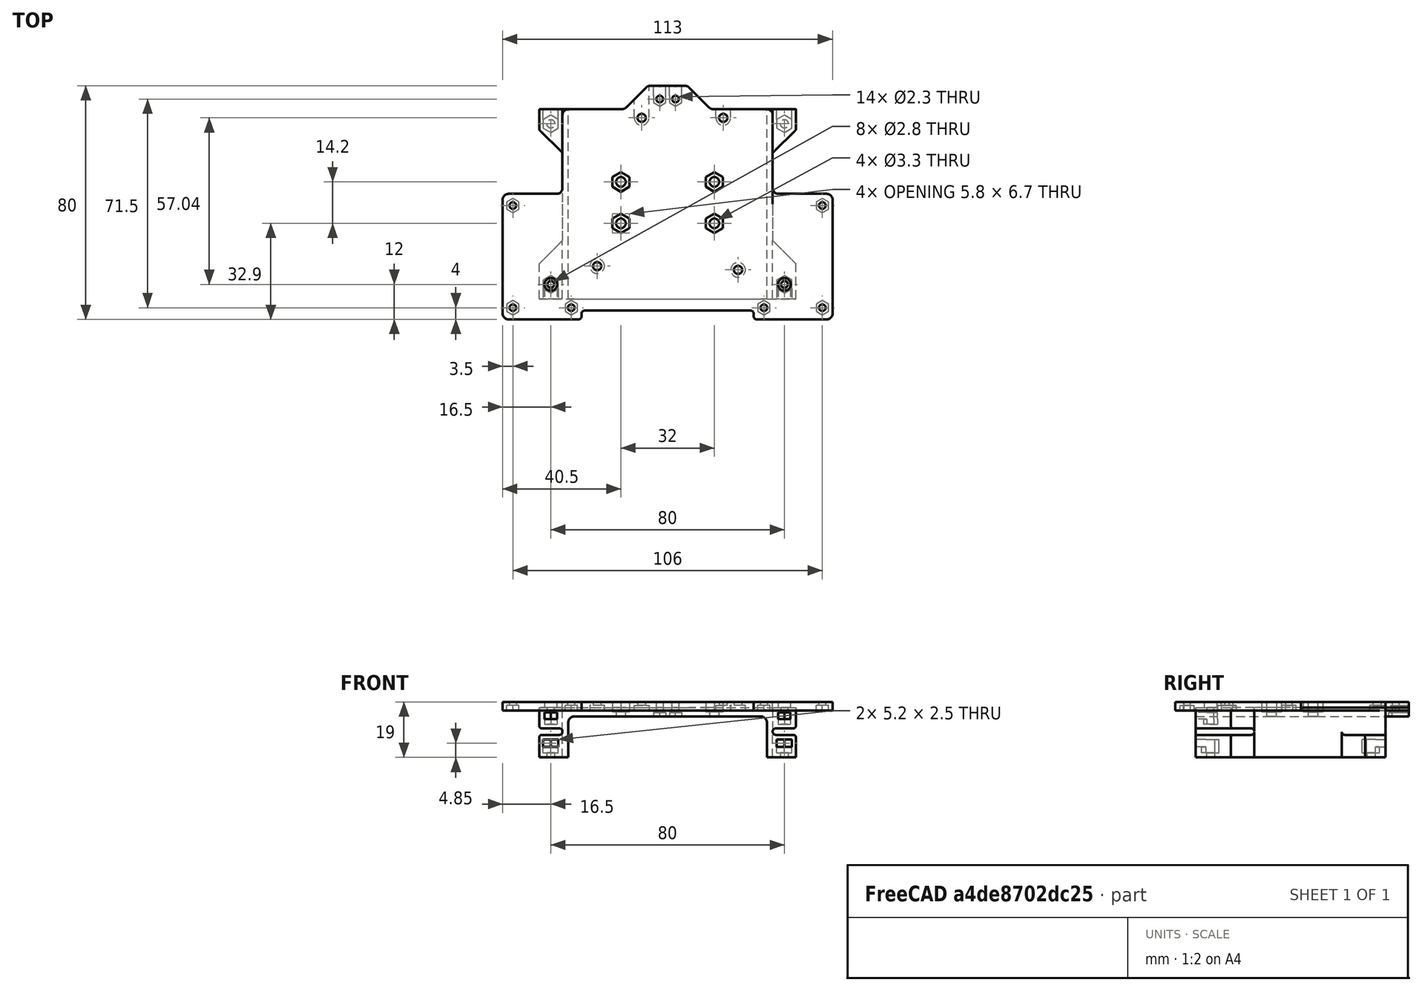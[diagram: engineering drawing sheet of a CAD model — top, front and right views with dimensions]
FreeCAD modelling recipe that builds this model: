
FCSTD DOCUMENT  (FreeCAD 0.19R24276 (Git))
Label: PB3D_TriPlate_BatBox
License: All rights reserved
LicenseURL: http://en.wikipedia.org/wiki/All_rights_reserved
objects: Sketcher::SketchObject×24, PartDesign::Pocket×18, PartDesign::Plane×7, PartDesign::Pad×2, PartDesign::Body×2, App::Part×2, Mesh::Feature×2, Spreadsheet::Sheet×1
note: 73 computed .brp shape members not serialized (recipe doc carries the construction recipe); baked Part::Feature solids carry a one-line shape summary decoded from their .brp

FEATURE [Spreadsheet::Sheet] Spreadsheet  label="params"
  cells = A2=M2 Bolt Clearances; C2=M2.5 Bolt Clearances; E2=M3 Bolt Clearances; A3=Hole Clear Diam; B3(m2_hole_clear_diam)==2.3mm; C3=Hole Clear Diam; D3(m25_hole_clear_diam)==2.8mm; E3=Hole Clear Diam; F3(m3_hole_clear_diam)==3.3mm; A4=Head Clear Diam; B4(m2_head_clear_diam)==4.3mm; C4=Head Clear Diam; D4(m25_head_clear_diam)==5mm; E4=Head Clear Diam; F4(m3_head_clear_diam)==6.1mm; A5=Head Min Depth; B5(m2_head_min_depth)==1.8mm; C5=Head Min Depth; D5(m25_head_min_depth)==2mm; E5=Head Min Depth; F5(m3_head_min_depth)==1.8mm; A6=Nut Clear Flat; B6(m2_nut_clear_flat)==4.2mm; C6=Nut Clear Flat; D6(m25_nut_clear_flat)==5.2mm; E6=Nut Clear Flat; F6(m3_nut_clear_flat)==5.8mm; A7=Nut Min Depth; B7(m2_nut_min_depth)==1.8mm; C7=Nut Min Depth; D7(m25_nut_min_depth)==2mm; E7=Nut Min Depth; F7(m3_nut_min_depth)==2.4mm; A9=BattBox Dims; C9=BattBox Foot; E9=BattBox Mt; G9=BattBox Batt Mt; I9=BBToMCP Read Overhang Mts; A10=Std. Rad.; B10(std_rad)==2mm; C10=Box Foot Width; D10(box_foot_width)==8mm; E10=Box Mt Offset L; F10(box_mt_offset_leng)==5mm; G10=Batt Mt Loc L; H10(bat_mt_loc_l)==25.9mm; I10=BB-MCP Rear Overhang Leng; J10(bbtomcp_rear_overhang_leng)==8mm; A11=Box Wall Thick; B11(box_wall_thick)==2mm; C11=Box Foot Height; D11(box_foot_height)==2 * box_mt_csunk_z + box_mt_csunk_depth + box_mt_slot_depth; E11=Box Mt Offset W; F11(box_mt_offset_width)==4mm; G11=Batt Mt Loc W; H11(bat_mt_loc_w)==16mm; I11=BB-MCP Rear Overhang Width; J11(bbtomcp_rear_overhang_width)==2 * m2_nut_clear_flat + 3 * bbtomcp_rear_hole_clearance; A12=Box Top Thick; B12(box_top_thick)==3mm; C12=Box Foot Front Leng; D12(box_foot_front_leng)==20mm; E12=Box Mt Leng; F12(box_mt_leng)==box_leng_tot - 2 * box_mt_offset_leng; G12=Batt Mt Space; H12(bat_mt_space)==14.2mm; I12=BB-MCP Rear Hole Space Clearance; J12(bbtomcp_rear_hole_clearance)==1.2mm; A13=Box Leng; B13(box_leng)==62mm; C13=Box Foot Back Leng; D13(box_foot_back_leng)==12mm; E13=Box Mt Width; F13(box_mt_width)==box_width_tot - 2 * box_mt_offset_width; G13=Batt Mt CSunk Depth; H13(bat_mt_csunk_depth)==1.5mm; I13=BB-MCP Rear Hole Spacing Width; J13(bbtomcp_rear_hole_spacing_width)==m2_nut_clear_flat + bbtomcp_rear_hole_clearance; A14=Box Width; B14(box_width)==64mm; C14=Box Foot Vert Split; D14(box_foot_vert_split)==2.2mm; E14=Box Mt CSunk Z ; F14(box_mt_csunk_z)==1.6mm; G14=BBToMCP Mts; I14=BB-MCP Rear Hole Offset; J14(bbtomcp_rear_hole_offset_leng)==4.5mm; A15=Box Height; B15(box_height)==14mm; C15=Box Leng Tot; D15(box_leng_tot)==box_leng + box_leng_overhang; E15=Box Mt CSunk Depth; F15(box_mt_csunk_depth)==m25_nut_min_depth; G15=BB-MCP Int Hole Loc L; H15(bbtomcp_hole_loc_leng)==box_mt_offset_leng; A16=Box Overhang; B16(box_leng_overhang)==3mm; C16=Box Width Tot; D16(box_width_tot)==box_width + 2 * std_rad + 2 * box_wall_thick + 2 * box_foot_width; E16=Box Mt Slot Z; F16(box_mt_slot_z)==box_mt_csunk_z + box_mt_csunk_depth; G16=BB-MCP Int Hole Loc Width; H16(bbtomcp_hole_space_width)==box_mt_width; A17=Batt Mt Hex Thru Loc; B17(bat_mt_hexthru_loc)==mcp_cent_leng - box_leng_tot; C17=Box Height Tot; D17(box_height_tot)==box_height + box_top_thick; E17=Box Mt Slot Depth; F17(box_mt_slot_depth)==m25_nut_min_depth + 0.5mm; G17=BB-MCP Int Hole Space Leng; H17(bbtomcp_hole_space_leng)==box_leng_tot + bbtomcp_rear_overhang_leng; A18=MuC Mt Plate; C18=MuC Mt Plate; E18=MuCP Aruino Mts; G18=BBToMCP Mts; A19=Cent Plate Leng; B19(mcp_cent_leng)==69mm; C19=Side Plate Offset Front Leng; D19(mcp_side_offset_front_leng)==3mm; E19=M4 L; F19(mm4_l)==2.7 * 25.4mm; G19=BB-MCP HexSlot Offset Z; H19(bbtomcp_hex_slot_offset_z)==1.6mm; A20=Cent Plate Width; B20(mcp_cent_width)==mcp_tot_width - 2 * mcp_side_width_offset; C20=Side Plate Offset Back Leng; D20(mcp_side_offset_back_leng)==29mm; E20=M4 W; F20(mm4_w)==2.1 * 25.4mm; G20=BB-MCP HexSlot Z; H20(bbtomcp_hex_slot_z)==box_height_tot - bbtomcp_hex_slot_offset_z; A21=Cent Plate Thick; B21(mcp_cent_thick)==3mm; C21=Side Plate Leng; D21(mcp_side_leng)==mcp_tot_leng - mcp_side_offset_front_leng; E21=M4 H1 W; F21(mm4_h1_w)==mm4_w / 2 - 0.1 * 25.4mm; G21=BB-MCP HexSlot Depth; H21(bbtomcp_hex_slot_height)==m2_nut_min_depth + 0.5mm; A22=Cent Plate Overhang; B22(mcp_cent_overhang)==mcp_cent_leng - box_leng_tot; C22=Side Plate Offset Width; D22(mcp_side_width_offset)==12.5mm; E22=M4 H1 L; F22(mm4_h1_l)==0.55 * 25.4mm; G22=BB-MCP HexSunk Z; H22(bbtomcp_hex_sunk_z)==bbtomcp_hex_slot_z - bbtomcp_hex_slot_height; A23=Tot Plate Leng; B23(mcp_tot_leng)==mcp_cent_leng + mcp_side_offset_front_leng; C23=Side Plate Width; D23(mcp_side_width)==27mm; E23=M4 H2 W; F23(mm4_h2_w)==mm4_w / 2 - 0.3 * 25.4mm; G23=BB-MCP HexSunk Height; H23(bbtomcp_hex_sunk_height)==m2_nut_min_depth; A24=Tot Plate Width; B24(mcp_tot_width)==113mm; E24=M4 H2 L; F24(mm4_h2_l)==mm4_l - 0.1 * 25.4mm; G24=BB-MCP Tot Height ; H24(bbtomcp_tot_height)==bbtomcp_hex_slot_offset_z + bbtomcp_hex_slot_height + bbtomcp_hex_sunk_height; C25=Xiao Mt Width; D25(mcp_xiaomt_width)==20mm; E25=M4 H3 W; F25(mm4_h3_w)==mm4_w / 2 - 0.7 * 25.4mm; G25=BB-MCP Leng Diff; H25(bbtomcp_leng_diff)==mcp_cent_leng - box_leng_tot; C26=Xiao Mt Leng; D26(mcp_xiaomt_leng)==35mm; E26=M4 H3 L; F26(mm4_h3_l)==mm4_l - 0.1 * 25.4mm; G26=MCP Rear Mt Leng; H26(mcp_rear_mt_leng)==7mm; C27=Xiao Mt Edge Clear W; D27(mcp_xiaomt_edgeclear_w)==3.5mm; E27=M4 H4 W; F27(mm4_h4_w)==mm4_w / 2 - 0.1 * 25.4mm; C28=Xiao Mt Edge Clear L; D28(mcp_xiaomt_edgeclear_l)==4mm; E28=M4 H4 L; F28(mm4_h4_l)==0.6 * 25.4mm; E29=M4 CSunk Depth; F29(mm4_csunk_depth)==1.8mm
FEATURE [Sketcher::SketchObject] Sketch
  FullyConstrained = true
  MapMode = 5
  Placement = pos=(0,0,0) rot=(1,0,0;1.5708rad)
  Support = -> [XZ_Plane001]
  expr: Constraints[67] = <<params>>.box_foot_vert_split
  expr: Constraints[68] = <<params>>.std_rad
  expr: Constraints[58] = <<params>>.box_wall_thick
  expr: Constraints[37] = <<params>>.box_height
  expr: Constraints[41] = <<params>>.std_rad / 2
  expr: Constraints[36] = <<params>>.box_top_thick
  expr: Constraints[32] = <<params>>.box_width
  expr: Constraints[38] = <<params>>.box_foot_width
  expr: Constraints[39] = Spreadsheet.box_foot_height
  sketch-geometry (29):
    g0: LineSegment StartX=-44 StartY=0 StartZ=0 EndX=-34 EndY=0 EndZ=0
    g1: LineSegment StartX=34 StartY=0 StartZ=0 EndX=44 EndY=0 EndZ=0
    g2: LineSegment StartX=-34 StartY=0 StartZ=0 EndX=-34 EndY=12 EndZ=0
    g3: LineSegment StartX=-32 StartY=14 StartZ=0 EndX=32 EndY=14 EndZ=0
    g4: LineSegment StartX=34 StartY=0 StartZ=0 EndX=34 EndY=12 EndZ=0
    g5: LineSegment StartX=44 StartY=0 StartZ=0 EndX=44 EndY=6.7 EndZ=0
    g6: LineSegment StartX=43 StartY=7.7 StartZ=0 EndX=37 EndY=7.7 EndZ=0
    g7: LineSegment StartX=36 StartY=8.7 StartZ=0 EndX=36 EndY=8.9 EndZ=0
    g8: LineSegment StartX=-44 StartY=0 StartZ=0 EndX=-44 EndY=6.7 EndZ=0
    g9: LineSegment StartX=-43 StartY=7.7 StartZ=0 EndX=-37 EndY=7.7 EndZ=0
    g10: LineSegment StartX=-36 StartY=8.7 StartZ=0 EndX=-36 EndY=8.9 EndZ=0
    g11: LineSegment StartX=-44 StartY=17 StartZ=0 EndX=44 EndY=17 EndZ=0
    g12: ArcOfCircle CenterX=-43 CenterY=6.7 CenterZ=0 NormalX=0 NormalY=0 NormalZ=1 AngleXU=0 Radius=1 StartAngle=1.5708 EndAngle=3.14159
    g13: ArcOfCircle CenterX=-37 CenterY=8.7 CenterZ=0 NormalX=0 NormalY=0 NormalZ=1 AngleXU=0 Radius=1 StartAngle=4.71239 EndAngle=6.28319
    g14: ArcOfCircle CenterX=37 CenterY=8.7 CenterZ=0 NormalX=0 NormalY=0 NormalZ=1 AngleXU=0 Radius=1 StartAngle=3.14159 EndAngle=4.71239
    g15: ArcOfCircle CenterX=43 CenterY=6.7 CenterZ=0 NormalX=0 NormalY=0 NormalZ=1 AngleXU=0 Radius=1 StartAngle=0 EndAngle=1.5708
    g16: ArcOfCircle CenterX=-32 CenterY=12 CenterZ=0 NormalX=0 NormalY=0 NormalZ=1 AngleXU=0 Radius=2 StartAngle=1.5708 EndAngle=3.14159
    g17: ArcOfCircle CenterX=32 CenterY=12 CenterZ=0 NormalX=0 NormalY=0 NormalZ=1 AngleXU=0 Radius=2 StartAngle=0 EndAngle=1.5708
    g18: LineSegment StartX=0 StartY=0 StartZ=0 EndX=0 EndY=17 EndZ=0
    g19: LineSegment StartX=-37 StartY=9.9 StartZ=0 EndX=-43 EndY=9.9 EndZ=0
    g20: LineSegment StartX=-44 StartY=10.9 StartZ=0 EndX=-44 EndY=17 EndZ=0
    g21: ArcOfCircle CenterX=-43 CenterY=10.9 CenterZ=0 NormalX=0 NormalY=0 NormalZ=1 AngleXU=0 Radius=1 StartAngle=3.14159 EndAngle=4.71239
    g22: ArcOfCircle CenterX=-37 CenterY=8.9 CenterZ=0 NormalX=0 NormalY=0 NormalZ=1 AngleXU=0 Radius=1 StartAngle=2e-16 EndAngle=1.5708
    g23: LineSegment StartX=44 StartY=17 StartZ=0 EndX=44 EndY=10.9 EndZ=0
    g24: LineSegment StartX=37 StartY=9.9 StartZ=0 EndX=43 EndY=9.9 EndZ=0
    g25: ArcOfCircle CenterX=43 CenterY=10.9 CenterZ=0 NormalX=0 NormalY=0 NormalZ=1 AngleXU=0 Radius=1 StartAngle=4.71239 EndAngle=6.28319
    g26: ArcOfCircle CenterX=37 CenterY=8.9 CenterZ=0 NormalX=0 NormalY=0 NormalZ=1 AngleXU=0 Radius=1 StartAngle=1.5708 EndAngle=3.14159
    g27: LineSegment StartX=-44 StartY=10.9 StartZ=0 EndX=-44 EndY=6.7 EndZ=0
    g28: LineSegment StartX=44 StartY=10.9 StartZ=0 EndX=44 EndY=6.7 EndZ=0
  constraints (73):
    c: PointOnObject(g0,g-1)
    c: PointOnObject(g0,g-1)
    c: Horizontal(g1)
    c: Equal(g0,g1)
    c: Symmetric(g0,g1,g-1)
    c: Coincident(g2,g0)
    c: Vertical(g2)
    c: Horizontal(g3)
    c: Coincident(g4,g1)
    c: Vertical(g4)
    c: Coincident(g5,g1)
    c: Vertical(g5)
    c: Horizontal(g6)
    c: Vertical(g7)
    c: Coincident(g8,g0)
    c: Vertical(g8)
    c: Horizontal(g9)
    c: Vertical(g10)
    c: Horizontal(g11)
    c: Tangent(g8,g12) = 1.5708
    c: Tangent(g9,g12) = 1.5708
    c: Tangent(g9,g13) = -1.5708
    c: Tangent(g10,g13) = -1.5708
    c: Tangent(g7,g14) = 1.5708
    c: Tangent(g6,g14) = 1.5708
    c: Tangent(g6,g15) = -1.5708
    c: Tangent(g5,g15) = -1.5708
    c: Tangent(g2,g16) = 1.5708
    c: Tangent(g3,g16) = 1.5708
    c: Tangent(g3,g17) = 1.5708
    c: Tangent(g4,g17) = -1.5708
    c: Equal(g17,g16)
    c: DistanceX(g3,g3) = 64
    c: Coincident(g18,g-1)
    c: PointOnObject(g18,g-2)
    c: Symmetric(g11,g11,g18)
    c: DistanceY(g3,g11) = 3
    c: DistanceY(g1,g3) = 14
    c: DistanceX(g7,g1) = 8
    c: DistanceY(g0,g9) = 7.7
    c: Equal(g8,g5)
    c: Radius(g14) = 1
    c: Equal(g6,g9)
    c: Equal(g13,g14)
    c: Horizontal(g19)
    c: Coincident(g20,g11)
    c: Vertical(g20)
    c: Tangent(g20,g21) = 1.5708
    c: Tangent(g19,g21) = 1.5708
    c: Tangent(g19,g22) = -1.5708
    c: Tangent(g10,g22) = -1.5708
    c: Coincident(g23,g11)
    c: Vertical(g23)
    c: Horizontal(g24)
    c: Tangent(g24,g25) = -1.5708
    c: Tangent(g23,g25) = 1.5708
    c: Tangent(g24,g26) = 1.5708
    c: Tangent(g7,g26) = 1.5708
    c: DistanceX(g1,g7) = 2
    c: Equal(g19,g24)
    c: Equal(g20,g23)
    c: Equal(g13,g22)
    c: Coincident(g27,g8)
    c: Coincident(g27,g20)
    c: Coincident(g28,g23)
    c: Coincident(g28,g5)
    c: Vertical(g28)
    c: DistanceY(g6,g24) = 2.2
    c: Radius(g17) = 2
    c: Equal(g14,g26)
    c: Equal(g14,g15)
    c: Equal(g25,g26)
    c: Equal(g22,g21)
FEATURE [PartDesign::Pad] Pad  label="MainBoxExt"
  Direction = (1,1,1)
  Length = 73
  Length2 = 100
  Placement = pos=(0,0,0) rot=(1,0,0;1.5708rad)
  Profile = -> Sketch
  Reversed = true
  Type = 0
  expr: Length = <<params>>.box_leng + <<params>>.box_leng_overhang + <<params>>.bbtomcp_rear_overhang_leng
FEATURE [Sketcher::SketchObject] Sketch001
  FullyConstrained = true
  MapMode = 5
  Support = -> [XY_Plane001]
  expr: Constraints[33] = <<params>>.box_width + 2 * <<params>>.box_wall_thick + 2 * <<params>>.std_rad
  expr: Constraints[34] = <<params>>.box_foot_front_leng
  expr: Constraints[35] = <<params>>.box_leng - <<params>>.box_foot_back_leng
  sketch-geometry (14):
    g0: LineSegment StartX=-66 StartY=80 StartZ=0 EndX=-36 EndY=50 EndZ=0
    g1: LineSegment StartX=-36 StartY=50 StartZ=0 EndX=-36 EndY=20 EndZ=0
    g2: LineSegment StartX=-36 StartY=20 StartZ=0 EndX=-66 EndY=-10 EndZ=0
    g3: LineSegment StartX=36 StartY=20 StartZ=0 EndX=66 EndY=-10 EndZ=0
    g4: LineSegment StartX=66 StartY=-10 StartZ=0 EndX=66 EndY=80 EndZ=0
    g5: LineSegment StartX=36 StartY=50 StartZ=0 EndX=66 EndY=80 EndZ=0
    g6: LineSegment StartX=36 StartY=50 StartZ=0 EndX=36 EndY=20 EndZ=0
    g7: LineSegment StartX=-66 StartY=80 StartZ=0 EndX=-66 EndY=-10 EndZ=0
    g8: LineSegment StartX=-66 StartY=-10 StartZ=0 EndX=66 EndY=-10 EndZ=0
    g9: LineSegment StartX=-36 StartY=20 StartZ=0 EndX=36 EndY=20 EndZ=0
    g10: LineSegment StartX=-36 StartY=50 StartZ=0 EndX=36 EndY=50 EndZ=0
    g11: LineSegment StartX=-66 StartY=80 StartZ=0 EndX=66 EndY=80 EndZ=0
    g12: LineSegment StartX=0 StartY=0 StartZ=0 EndX=0 EndY=-10 EndZ=0
    g13: LineSegment StartX=0 StartY=0 StartZ=0 EndX=0 EndY=20 EndZ=0
  constraints (36):
    c: Coincident(g1,g0)
    c: Vertical(g1)
    c: Coincident(g2,g1)
    c: Coincident(g4,g3)
    c: Vertical(g4)
    c: Coincident(g5,g4)
    c: Coincident(g6,g5)
    c: Coincident(g6,g3)
    c: Vertical(g6)
    c: Coincident(g7,g0)
    c: Coincident(g7,g2)
    c: Vertical(g7)
    c: Coincident(g8,g2)
    c: Coincident(g8,g3)
    c: Horizontal(g8)
    c: Coincident(g9,g1)
    c: Coincident(g9,g3)
    c: Horizontal(g9)
    c: Coincident(g10,g0)
    c: Coincident(g10,g5)
    c: Coincident(g11,g0)
    c: Coincident(g11,g4)
    c: Horizontal(g11)
    c: Coincident(g12,g-1)
    c: PointOnObject(g12,g-2)
    c: Coincident(g13,g-1)
    c: PointOnObject(g13,g-2)
    c: Symmetric(g2,g3,g12)
    c: Symmetric(g1,g3,g13)
    c: Horizontal(g10)
    c: Equal(g2,g0)
    c: Angle(g3,g8) = 0.785398
    c: DistanceX(g3,g3) = 30
    c: DistanceX(g1,g3) = 72
    c: DistanceY(g-1,g3) = 20
    c: DistanceY(g-1,g5) = 50
FEATURE [PartDesign::Pocket] Pocket  label="FootAngleCut"
  BaseFeature = -> Pad
  Length = 8.7
  Length2 = 100
  Placement = pos=(0,0,0) rot=(1,0,0;1.5708rad)
  Profile = -> Sketch001
  Reversed = true
  Type = 1
  expr: Length = <<params>>.box_foot_height + <<params>>.std_rad / 2
FEATURE [Sketcher::SketchObject] Sketch002  label="Sketch_MtHoleTemplate"
  FullyConstrained = true
  MapMode = 5
  Support = -> [XY_Plane001]
  expr: Constraints[11] = <<params>>.box_mt_offset_leng
  expr: Constraints[12] = <<params>>.box_mt_leng
  expr: Constraints[13] = <<params>>.box_mt_width
  sketch-geometry (5):
    g0: LineSegment StartX=-40 StartY=60 StartZ=0 EndX=40 EndY=60 EndZ=0
    g1: LineSegment StartX=40 StartY=60 StartZ=0 EndX=40 EndY=5 EndZ=0
    g2: LineSegment StartX=40 StartY=5 StartZ=0 EndX=-40 EndY=5 EndZ=0
    g3: LineSegment StartX=-40 StartY=5 StartZ=0 EndX=-40 EndY=60 EndZ=0
    g4: LineSegment StartX=0 StartY=0 StartZ=0 EndX=0 EndY=5 EndZ=0
  constraints (14):
    c: Coincident(g0,g1)
    c: Coincident(g1,g2)
    c: Coincident(g2,g3)
    c: Coincident(g3,g0)
    c: Horizontal(g0)
    c: Horizontal(g2)
    c: Vertical(g1)
    c: Vertical(g3)
    c: Coincident(g4,g-1)
    c: PointOnObject(g4,g-2)
    c: Symmetric(g2,g1,g4)
    c: DistanceY(g-1,g4) = 5
    c: DistanceY(g1,g0) = 55
    c: DistanceX(g0,g0) = 80
FEATURE [PartDesign::Plane] DatumPlane  label="Datum_MtCSunkZ"
  AttachmentOffset = pos=(0,0,1.6) rot=(0,0,1;0rad)
  Length = 106.573
  MapMode = 5
  Placement = pos=(0,0,1.6) rot=(0,0,1;0rad)
  ResizeMode = 0
  Support = -> [XY_Plane001]
  Width = 116.573
  expr: .AttachmentOffset.Base.z = <<params>>.box_mt_csunk_z
FEATURE [PartDesign::Plane] DatumPlane001  label="Datum_MtSlotZ"
  AttachmentOffset = pos=(0,0,3.6) rot=(0,0,1;0rad)
  Length = 106.573
  MapMode = 5
  Placement = pos=(0,0,3.6) rot=(0,0,1;0rad)
  ResizeMode = 0
  Support = -> [XY_Plane001]
  Width = 116.573
  expr: .AttachmentOffset.Base.z = <<params>>.box_mt_slot_z
FEATURE [Sketcher::SketchObject] Sketch004  label="Sketch_Mt_CSunk"
  FullyConstrained = true
  MapMode = 5
  Placement = pos=(0,0,1.6) rot=(0,0,1;0rad)
  Support = -> [DatumPlane]
  expr: Constraints[13] = <<params>>.box_mt_width
  expr: Constraints[12] = <<params>>.box_mt_leng
  expr: Constraints[11] = <<params>>.box_mt_offset_leng
  expr: Constraints[93] = <<params>>.m25_nut_clear_flat
  sketch-geometry (33):
    g0: LineSegment StartX=-40 StartY=60 StartZ=0 EndX=40 EndY=60 EndZ=0
    g1: LineSegment StartX=40 StartY=60 StartZ=0 EndX=40 EndY=5 EndZ=0
    g2: LineSegment StartX=40 StartY=5 StartZ=0 EndX=-40 EndY=5 EndZ=0
    g3: LineSegment StartX=-40 StartY=5 StartZ=0 EndX=-40 EndY=60 EndZ=0
    g4: LineSegment StartX=0 StartY=0 StartZ=0 EndX=0 EndY=5 EndZ=0
    g5: LineSegment StartX=-40 StartY=1.99778 StartZ=0 EndX=-37.4 EndY=3.49889 EndZ=0
    g6: LineSegment StartX=-37.4 StartY=3.49889 StartZ=0 EndX=-37.4 EndY=6.50111 EndZ=0
    g7: LineSegment StartX=-37.4 StartY=6.50111 StartZ=0 EndX=-40 EndY=8.00222 EndZ=0
    g8: LineSegment StartX=-40 StartY=8.00222 StartZ=0 EndX=-42.6 EndY=6.50111 EndZ=0
    g9: LineSegment StartX=-42.6 StartY=6.50111 StartZ=0 EndX=-42.6 EndY=3.49889 EndZ=0
    g10: LineSegment StartX=-42.6 StartY=3.49889 StartZ=0 EndX=-40 EndY=1.99778 EndZ=0
    g11: Circle CenterX=-40 CenterY=5 CenterZ=0 NormalX=0 NormalY=0 NormalZ=1 AngleXU=0 Radius=3.00222
    g12: LineSegment StartX=40 StartY=1.99778 StartZ=0 EndX=42.6 EndY=3.49889 EndZ=0
    g13: LineSegment StartX=42.6 StartY=3.49889 StartZ=0 EndX=42.6 EndY=6.50111 EndZ=0
    g14: LineSegment StartX=42.6 StartY=6.50111 StartZ=0 EndX=40 EndY=8.00222 EndZ=0
    g15: LineSegment StartX=40 StartY=8.00222 StartZ=0 EndX=37.4 EndY=6.50111 EndZ=0
    g16: LineSegment StartX=37.4 StartY=6.50111 StartZ=0 EndX=37.4 EndY=3.49889 EndZ=0
    g17: LineSegment StartX=37.4 StartY=3.49889 StartZ=0 EndX=40 EndY=1.99778 EndZ=0
    g18: Circle CenterX=40 CenterY=5 CenterZ=0 NormalX=0 NormalY=0 NormalZ=1 AngleXU=0 Radius=3.00222
    g19: LineSegment StartX=40 StartY=56.9978 StartZ=0 EndX=42.6 EndY=58.4989 EndZ=0
    g20: LineSegment StartX=42.6 StartY=58.4989 StartZ=0 EndX=42.6 EndY=61.5011 EndZ=0
    g21: LineSegment StartX=42.6 StartY=61.5011 StartZ=0 EndX=40 EndY=63.0022 EndZ=0
    g22: LineSegment StartX=40 StartY=63.0022 StartZ=0 EndX=37.4 EndY=61.5011 EndZ=0
    g23: LineSegment StartX=37.4 StartY=61.5011 StartZ=0 EndX=37.4 EndY=58.4989 EndZ=0
    g24: LineSegment StartX=37.4 StartY=58.4989 StartZ=0 EndX=40 EndY=56.9978 EndZ=0
    g25: Circle CenterX=40 CenterY=60 CenterZ=0 NormalX=0 NormalY=0 NormalZ=1 AngleXU=0 Radius=3.00222
    g26: LineSegment StartX=-40 StartY=56.9978 StartZ=0 EndX=-37.4 EndY=58.4989 EndZ=0
    g27: LineSegment StartX=-37.4 StartY=58.4989 StartZ=0 EndX=-37.4 EndY=61.5011 EndZ=0
    g28: LineSegment StartX=-37.4 StartY=61.5011 StartZ=0 EndX=-40 EndY=63.0022 EndZ=0
    g29: LineSegment StartX=-40 StartY=63.0022 StartZ=0 EndX=-42.6 EndY=61.5011 EndZ=0
    g30: LineSegment StartX=-42.6 StartY=61.5011 StartZ=0 EndX=-42.6 EndY=58.4989 EndZ=0
    g31: LineSegment StartX=-42.6 StartY=58.4989 StartZ=0 EndX=-40 EndY=56.9978 EndZ=0
    g32: Circle CenterX=-40 CenterY=60 CenterZ=0 NormalX=0 NormalY=0 NormalZ=1 AngleXU=0 Radius=3.00222
  constraints (78):
    c: Coincident(g0,g1)
    c: Coincident(g1,g2)
    c: Coincident(g2,g3)
    c: Coincident(g3,g0)
    c: Horizontal(g0)
    c: Horizontal(g2)
    c: Vertical(g1)
    c: Vertical(g3)
    c: Coincident(g4,g-1)
    c: PointOnObject(g4,g-2)
    c: Symmetric(g2,g1,g4)
    c: DistanceY(g-1,g4) = 5
    c: DistanceY(g1,g0) = 55
    c: DistanceX(g0,g0) = 80
    c: Coincident(g5,g6)
    c: Coincident(g6,g7)
    c: Coincident(g7,g8)
    c: Coincident(g8,g9)
    c: Coincident(g9,g10)
    c: Coincident(g10,g5)
    c: Equal(g5, g6-g10) x5
    c: PointOnObject(g5,g11)
    c: PointOnObject(g6,g11)
    c: PointOnObject(g7,g11)
    c: PointOnObject(g8,g11)
    c: PointOnObject(g9,g11)
    c: PointOnObject(g10,g11)
    c: Coincident(g11,g2)
    c: Coincident(g12,g13)
    c: Coincident(g13,g14)
    c: Coincident(g14,g15)
    c: Coincident(g15,g16)
    c: Coincident(g16,g17)
    c: Coincident(g17,g12)
    c: Equal(g12, g13-g17) x5
    c: PointOnObject(g12,g18)
    c: PointOnObject(g13,g18)
    c: PointOnObject(g14,g18)
    c: PointOnObject(g15,g18)
    c: PointOnObject(g16,g18)
    c: PointOnObject(g17,g18)
    c: Coincident(g18,g1)
    c: Coincident(g19,g20)
    c: Coincident(g20,g21)
    c: Coincident(g21,g22)
    c: Coincident(g22,g23)
    c: Coincident(g23,g24)
    c: Coincident(g24,g19)
    c: Equal(g19, g20-g24) x5
    c: PointOnObject(g19,g25)
    c: PointOnObject(g20,g25)
    c: PointOnObject(g21,g25)
    c: PointOnObject(g22,g25)
    c: PointOnObject(g23,g25)
    c: PointOnObject(g24,g25)
    c: Coincident(g25,g0)
    c: Coincident(g26,g27)
    c: Coincident(g27,g28)
    c: Coincident(g28,g29)
    c: Coincident(g29,g30)
    c: Coincident(g30,g31)
    c: Coincident(g31,g26)
    c: Equal(g26, g27-g31) x5
    c: PointOnObject(g26,g32)
    c: PointOnObject(g27,g32)
    c: PointOnObject(g28,g32)
    c: PointOnObject(g29,g32)
    c: PointOnObject(g30,g32)
    c: PointOnObject(g31,g32)
    c: Coincident(g32,g0)
    c: Vertical(g30)
    c: Vertical(g23)
    c: Vertical(g13)
    c: Vertical(g6)
    c: Equal(g11,g18)
    c: Equal(g18,g25)
    c: Equal(g25,g32)
    c: DistanceX(g16,g12) = 5.2
FEATURE [Sketcher::SketchObject] Sketch005  label="Sketch_Mt_Slot"
  FullyConstrained = true
  MapMode = 5
  Placement = pos=(0,0,3.6) rot=(0,0,1;0rad)
  Support = -> [DatumPlane001]
  expr: Constraints[11] = <<params>>.box_mt_offset_leng
  expr: Constraints[13] = <<params>>.box_mt_width
  expr: Constraints[12] = <<params>>.box_mt_leng
  expr: Constraints[63] = <<params>>.m25_nut_clear_flat
  sketch-geometry (37):
    g0: LineSegment StartX=-40 StartY=60 StartZ=0 EndX=40 EndY=60 EndZ=0
    g1: LineSegment StartX=40 StartY=60 StartZ=0 EndX=40 EndY=5 EndZ=0
    g2: LineSegment StartX=40 StartY=5 StartZ=0 EndX=-40 EndY=5 EndZ=0
    g3: LineSegment StartX=-40 StartY=5 StartZ=0 EndX=-40 EndY=60 EndZ=0
    g4: LineSegment StartX=0 StartY=0 StartZ=0 EndX=0 EndY=5 EndZ=0
    g5: LineSegment StartX=-37.4 StartY=3.49889 StartZ=0 EndX=-37.4 EndY=6.50111 EndZ=0
    g6: LineSegment StartX=-37.4 StartY=6.50111 StartZ=0 EndX=-40 EndY=8.00222 EndZ=0
    g7: LineSegment StartX=-40 StartY=8.00222 StartZ=0 EndX=-42.6 EndY=6.50111 EndZ=0
    g8: LineSegment StartX=-42.6 StartY=6.50111 StartZ=0 EndX=-42.6 EndY=3.49889 EndZ=0
    g9: Circle CenterX=-40 CenterY=5 CenterZ=0 NormalX=0 NormalY=0 NormalZ=1 AngleXU=0 Radius=3.00222
    g10: LineSegment StartX=42.6 StartY=3.49889 StartZ=0 EndX=42.6 EndY=6.50111 EndZ=0
    g11: LineSegment StartX=42.6 StartY=6.50111 StartZ=0 EndX=40 EndY=8.00222 EndZ=0
    g12: LineSegment StartX=40 StartY=8.00222 StartZ=0 EndX=37.4 EndY=6.50111 EndZ=0
    g13: LineSegment StartX=37.4 StartY=6.50111 StartZ=0 EndX=37.4 EndY=3.49889 EndZ=0
    g14: Circle CenterX=40 CenterY=5 CenterZ=0 NormalX=0 NormalY=0 NormalZ=1 AngleXU=0 Radius=3.00222
    g15: LineSegment StartX=-40 StartY=56.9978 StartZ=0 EndX=-37.4 EndY=58.4989 EndZ=0
    g16: LineSegment StartX=-37.4 StartY=58.4989 StartZ=0 EndX=-37.4 EndY=61.5011 EndZ=0
    g17: LineSegment StartX=-42.6 StartY=61.5011 StartZ=0 EndX=-42.6 EndY=58.4989 EndZ=0
    g18: LineSegment StartX=-42.6 StartY=58.4989 StartZ=0 EndX=-40 EndY=56.9978 EndZ=0
    g19: Circle CenterX=-40 CenterY=60 CenterZ=0 NormalX=0 NormalY=0 NormalZ=1 AngleXU=0 Radius=3.00222
    g20: LineSegment StartX=37.4 StartY=58.4989 StartZ=0 EndX=40 EndY=56.9978 EndZ=0
    g21: LineSegment StartX=40 StartY=56.9978 StartZ=0 EndX=42.6 EndY=58.4989 EndZ=0
    g22: LineSegment StartX=42.6 StartY=58.4989 StartZ=0 EndX=42.6 EndY=61.5011 EndZ=0
    g23: LineSegment StartX=37.4 StartY=61.5011 StartZ=0 EndX=37.4 EndY=58.4989 EndZ=0
    g24: Circle CenterX=40 CenterY=60 CenterZ=0 NormalX=0 NormalY=0 NormalZ=1 AngleXU=0 Radius=3.00222
    g25: LineSegment StartX=-42.6 StartY=3.49889 StartZ=0 EndX=-42.6 EndY=-6.50111 EndZ=0
    g26: LineSegment StartX=-37.4 StartY=3.49889 StartZ=0 EndX=-37.4 EndY=-6.50111 EndZ=0
    g27: LineSegment StartX=-42.6 StartY=-6.50111 StartZ=0 EndX=-37.4 EndY=-6.50111 EndZ=0
    g28: LineSegment StartX=37.4 StartY=3.49889 StartZ=0 EndX=37.4 EndY=-6.50111 EndZ=0
    g29: LineSegment StartX=42.6 StartY=3.49889 StartZ=0 EndX=42.6 EndY=-6.50111 EndZ=0
    g30: LineSegment StartX=37.4 StartY=-6.50111 StartZ=0 EndX=42.6 EndY=-6.50111 EndZ=0
    g31: LineSegment StartX=37.4 StartY=61.5011 StartZ=0 EndX=37.4 EndY=71.5011 EndZ=0
    g32: LineSegment StartX=42.6 StartY=61.5011 StartZ=0 EndX=42.6 EndY=71.5011 EndZ=0
    g33: LineSegment StartX=37.4 StartY=71.5011 StartZ=0 EndX=42.6 EndY=71.5011 EndZ=0
    g34: LineSegment StartX=-42.6 StartY=61.5011 StartZ=0 EndX=-42.6 EndY=71.5011 EndZ=0
    g35: LineSegment StartX=-37.4 StartY=61.5011 StartZ=0 EndX=-37.4 EndY=71.5011 EndZ=0
    g36: LineSegment StartX=-42.6 StartY=71.5011 StartZ=0 EndX=-37.4 EndY=71.5011 EndZ=0
  constraints (106):
    c: Coincident(g0,g1)
    c: Coincident(g1,g2)
    c: Coincident(g2,g3)
    c: Coincident(g3,g0)
    c: Horizontal(g0)
    c: Horizontal(g2)
    c: Vertical(g1)
    c: Vertical(g3)
    c: Coincident(g4,g-1)
    c: PointOnObject(g4,g-2)
    c: Symmetric(g2,g1,g4)
    c: DistanceY(g-1,g4) = 5
    c: DistanceY(g1,g0) = 55
    c: DistanceX(g0,g0) = 80
    c: Coincident(g5,g6)
    c: Coincident(g6,g7)
    c: Coincident(g7,g8)
    c: PointOnObject(g5,g9)
    c: PointOnObject(g5,g9)
    c: PointOnObject(g6,g9)
    c: PointOnObject(g7,g9)
    c: PointOnObject(g8,g9)
    c: Coincident(g9,g2)
    c: Coincident(g10,g11)
    c: Coincident(g11,g12)
    c: Coincident(g12,g13)
    c: PointOnObject(g10,g14)
    c: PointOnObject(g10,g14)
    c: PointOnObject(g11,g14)
    c: PointOnObject(g12,g14)
    c: PointOnObject(g13,g14)
    c: Coincident(g14,g1)
    c: Coincident(g15,g16)
    c: Coincident(g17,g18)
    c: Coincident(g18,g15)
    c: Equal(g15,g16)
    c: Equal(g15,g17)
    c: Equal(g15,g18)
    c: PointOnObject(g15,g19)
    c: PointOnObject(g16,g19)
    c: PointOnObject(g17,g19)
    c: PointOnObject(g17,g19)
    c: PointOnObject(g18,g19)
    c: Coincident(g19,g0)
    c: Coincident(g20,g21)
    c: Coincident(g21,g22)
    c: Coincident(g23,g20)
    c: Equal(g20,g21)
    c: Equal(g20,g22)
    c: Equal(g20,g23)
    c: PointOnObject(g20,g24)
    c: PointOnObject(g21,g24)
    c: PointOnObject(g22,g24)
    c: PointOnObject(g23,g24)
    c: PointOnObject(g23,g24)
    c: Coincident(g24,g0)
    c: Vertical(g17)
    c: Vertical(g22)
    c: Vertical(g10)
    c: Vertical(g8)
    c: Equal(g9,g14)
    c: Equal(g14,g24)
    c: Equal(g24,g19)
    c: DistanceX(g13,g10) = 5.2
    c: Coincident(g25,g8)
    c: Vertical(g25)
    c: Coincident(g26,g5)
    c: Vertical(g26)
    c: Coincident(g27,g25)
    c: Coincident(g27,g26)
    c: Horizontal(g27)
    c: Vertical(g5)
    c: Vertical(g13)
    c: Coincident(g28,g13)
    c: Vertical(g28)
    c: Coincident(g29,g10)
    c: Vertical(g29)
    c: Coincident(g30,g28)
    c: Coincident(g30,g29)
    c: Horizontal(g30)
    c: Equal(g10,g11)
    c: Equal(g12,g11)
    c: Equal(g12,g13)
    c: DistanceY(g29,g10) = 10
    c: Equal(g8,g7)
    c: Equal(g7,g6)
    c: Equal(g6,g5)
    c: Equal(g28,g26)
    c: Vertical(g23)
    c: Coincident(g31,g23)
    c: Vertical(g31)
    c: Coincident(g32,g22)
    c: Vertical(g32)
    c: Coincident(g33,g31)
    c: Coincident(g33,g32)
    c: Horizontal(g33)
    c: Vertical(g16)
    c: Coincident(g34,g17)
    c: Vertical(g34)
    c: Coincident(g35,g16)
    c: Vertical(g35)
    c: Coincident(g36,g34)
    c: Coincident(g36,g35)
    c: Horizontal(g36)
    c: Equal(g28,g31)
    c: Equal(g35,g31)
FEATURE [Sketcher::SketchObject] Sketch006  label="Sketch_Mt_Holes"
  FullyConstrained = true
  MapMode = 5
  Support = -> [XY_Plane001]
  expr: Constraints[13] = <<params>>.box_mt_width
  expr: Constraints[12] = <<params>>.box_mt_leng
  expr: Constraints[11] = <<params>>.box_mt_offset_leng
  expr: Constraints[21] = <<params>>.m25_hole_clear_diam
  sketch-geometry (9):
    g0: LineSegment StartX=-40 StartY=60 StartZ=0 EndX=40 EndY=60 EndZ=0
    g1: LineSegment StartX=40 StartY=60 StartZ=0 EndX=40 EndY=5 EndZ=0
    g2: LineSegment StartX=40 StartY=5 StartZ=0 EndX=-40 EndY=5 EndZ=0
    g3: LineSegment StartX=-40 StartY=5 StartZ=0 EndX=-40 EndY=60 EndZ=0
    g4: LineSegment StartX=0 StartY=0 StartZ=0 EndX=0 EndY=5 EndZ=0
    g5: Circle CenterX=-40 CenterY=60 CenterZ=0 NormalX=0 NormalY=0 NormalZ=1 AngleXU=0 Radius=1.4
    g6: Circle CenterX=40 CenterY=60 CenterZ=0 NormalX=0 NormalY=0 NormalZ=1 AngleXU=0 Radius=1.4
    g7: Circle CenterX=40 CenterY=5 CenterZ=0 NormalX=0 NormalY=0 NormalZ=1 AngleXU=0 Radius=1.4
    g8: Circle CenterX=-40 CenterY=5 CenterZ=0 NormalX=0 NormalY=0 NormalZ=1 AngleXU=0 Radius=1.4
  constraints (22):
    c: Coincident(g0,g1)
    c: Coincident(g1,g2)
    c: Coincident(g2,g3)
    c: Coincident(g3,g0)
    c: Horizontal(g0)
    c: Horizontal(g2)
    c: Vertical(g1)
    c: Vertical(g3)
    c: Coincident(g4,g-1)
    c: PointOnObject(g4,g-2)
    c: Symmetric(g2,g1,g4)
    c: DistanceY(g-1,g4) = 5
    c: DistanceY(g1,g0) = 55
    c: DistanceX(g0,g0) = 80
    c: Coincident(g5,g0)
    c: Coincident(g6,g0)
    c: Coincident(g7,g1)
    c: Coincident(g8,g2)
    c: Equal(g5,g8)
    c: Equal(g8,g6)
    c: Equal(g6,g7)
    c: Diameter(g7) = 2.8
FEATURE [PartDesign::Pocket] Pocket001  label="MtHoles"
  BaseFeature = -> Pocket
  Length = 5.7
  Length2 = 100
  Placement = pos=(0,0,0) rot=(1,0,0;1.5708rad)
  Profile = -> Sketch006
  Reversed = true
  Type = 0
  expr: Length = <<params>>.box_foot_height - <<params>>.box_wall_thick
FEATURE [PartDesign::Pocket] Pocket002  label="MtSlot"
  BaseFeature = -> Pocket001
  Length = 2.5
  Length2 = 100
  Placement = pos=(0,0,0) rot=(1,0,0;1.5708rad)
  Profile = -> Sketch005
  Reversed = true
  Type = 0
  expr: Length = <<params>>.box_mt_slot_depth
FEATURE [PartDesign::Pocket] Pocket003  label="MtCSunk"
  BaseFeature = -> Pocket002
  Length = 2
  Length2 = 100
  Placement = pos=(0,0,0) rot=(1,0,0;1.5708rad)
  Profile = -> Sketch004
  Reversed = true
  Type = 0
  expr: Length = <<params>>.box_mt_csunk_depth
FEATURE [PartDesign::Plane] DatumPlane002  label="Datum_BoxTop"
  AttachmentOffset = pos=(0,0,17) rot=(0,0,1;0rad)
  Length = 106.573
  MapMode = 5
  Placement = pos=(0,0,17) rot=(0,0,1;0rad)
  ResizeMode = 0
  Support = -> [XY_Plane001]
  Width = 116.573
  expr: .AttachmentOffset.Base.z = <<params>>.box_height_tot
FEATURE [Sketcher::SketchObject] Sketch007  label="Sketch_BattMtHoles"
  FullyConstrained = true
  MapMode = 5
  Support = -> [XY_Plane001]
  expr: Constraints[18] = <<params>>.m3_hole_clear_diam
  sketch-geometry (9):
    g0: Circle CenterX=-16 CenterY=40.1 CenterZ=0 NormalX=0 NormalY=0 NormalZ=1 AngleXU=0 Radius=1.65
    g1: Circle CenterX=-16 CenterY=25.9 CenterZ=0 NormalX=0 NormalY=0 NormalZ=1 AngleXU=0 Radius=1.65
    g2: Circle CenterX=16 CenterY=40.1 CenterZ=0 NormalX=0 NormalY=0 NormalZ=1 AngleXU=0 Radius=1.65
    g3: Circle CenterX=16 CenterY=25.9 CenterZ=0 NormalX=0 NormalY=0 NormalZ=1 AngleXU=0 Radius=1.65
    g4: LineSegment StartX=-16 StartY=40.1 StartZ=0 EndX=-16 EndY=25.9 EndZ=0
    g5: LineSegment StartX=16 StartY=40.1 StartZ=0 EndX=16 EndY=25.9 EndZ=0
    g6: LineSegment StartX=-16 StartY=25.9 StartZ=0 EndX=16 EndY=25.9 EndZ=0
    g7: LineSegment StartX=0 StartY=0 StartZ=0 EndX=0 EndY=25.9 EndZ=0
    g8: LineSegment StartX=-16 StartY=40.1 StartZ=0 EndX=16 EndY=40.1 EndZ=0
  constraints (22):
    c: Coincident(g4,g0)
    c: Coincident(g4,g1)
    c: Coincident(g5,g2)
    c: Coincident(g5,g3)
    c: Vertical(g4)
    c: Vertical(g5)
    c: Coincident(g6,g1)
    c: Coincident(g6,g3)
    c: Horizontal(g6)
    c: Coincident(g7,g-1)
    c: PointOnObject(g7,g-2)
    c: Symmetric(g1,g3,g7)
    c: Coincident(g8,g0)
    c: Coincident(g8,g2)
    c: Horizontal(g8)
    c: Equal(g3,g1)
    c: Equal(g3,g2)
    c: Equal(g3,g0)
    c: Diameter(g2) = 3.3
    c: DistanceY(g3,g2) = 14.2
    c: DistanceY(g-1,g3) = 25.9
    c: DistanceX(g0,g2) = 32
FEATURE [PartDesign::Pocket] Pocket004  label="BattMtHoles"
  BaseFeature = -> Pocket003
  Length = 5
  Length2 = 100
  Placement = pos=(0,0,0) rot=(1,0,0;1.5708rad)
  Profile = -> Sketch007
  Reversed = true
  Type = 1
FEATURE [Sketcher::SketchObject] Sketch008  label="Sketch_BattMtHexSunk"
  FullyConstrained = true
  MapMode = 5
  Placement = pos=(0,0,17) rot=(0,0,1;0rad)
  Support = -> [DatumPlane002]
  expr: Constraints[7] = <<params>>.bat_mt_space
  expr: Constraints[6] = <<params>>.bat_mt_loc_l
  expr: Constraints[93] = <<params>>.bat_mt_loc_w
  expr: Constraints[91] = <<params>>.m3_nut_clear_flat
  sketch-geometry (33):
    g0: LineSegment StartX=-16 StartY=40.1 StartZ=0 EndX=-16 EndY=25.9 EndZ=0
    g1: LineSegment StartX=16 StartY=40.1 StartZ=0 EndX=16 EndY=25.9 EndZ=0
    g2: LineSegment StartX=-16 StartY=25.9 StartZ=0 EndX=16 EndY=25.9 EndZ=0
    g3: LineSegment StartX=0 StartY=0 StartZ=0 EndX=0 EndY=25.9 EndZ=0
    g4: LineSegment StartX=-16 StartY=40.1 StartZ=0 EndX=16 EndY=40.1 EndZ=0
    g5: LineSegment StartX=-18.9 StartY=41.7743 StartZ=0 EndX=-18.9 EndY=38.4257 EndZ=0
    g6: LineSegment StartX=-18.9 StartY=38.4257 StartZ=0 EndX=-16 EndY=36.7514 EndZ=0
    g7: LineSegment StartX=-16 StartY=36.7514 StartZ=0 EndX=-13.1 EndY=38.4257 EndZ=0
    g8: LineSegment StartX=-13.1 StartY=38.4257 StartZ=0 EndX=-13.1 EndY=41.7743 EndZ=0
    g9: LineSegment StartX=-13.1 StartY=41.7743 StartZ=0 EndX=-16 EndY=43.4486 EndZ=0
    g10: LineSegment StartX=-16 StartY=43.4486 StartZ=0 EndX=-18.9 EndY=41.7743 EndZ=0
    g11: Circle CenterX=-16 CenterY=40.1 CenterZ=0 NormalX=0 NormalY=0 NormalZ=1 AngleXU=0 Radius=3.34863
    g12: LineSegment StartX=13.1 StartY=41.7743 StartZ=0 EndX=13.1 EndY=38.4257 EndZ=0
    g13: LineSegment StartX=13.1 StartY=38.4257 StartZ=0 EndX=16 EndY=36.7514 EndZ=0
    g14: LineSegment StartX=16 StartY=36.7514 StartZ=0 EndX=18.9 EndY=38.4257 EndZ=0
    g15: LineSegment StartX=18.9 StartY=38.4257 StartZ=0 EndX=18.9 EndY=41.7743 EndZ=0
    g16: LineSegment StartX=18.9 StartY=41.7743 StartZ=0 EndX=16 EndY=43.4486 EndZ=0
    g17: LineSegment StartX=16 StartY=43.4486 StartZ=0 EndX=13.1 EndY=41.7743 EndZ=0
    g18: Circle CenterX=16 CenterY=40.1 CenterZ=0 NormalX=0 NormalY=0 NormalZ=1 AngleXU=0 Radius=3.34863
    g19: LineSegment StartX=-18.9 StartY=27.5743 StartZ=0 EndX=-18.9 EndY=24.2257 EndZ=0
    g20: LineSegment StartX=-18.9 StartY=24.2257 StartZ=0 EndX=-16 EndY=22.5514 EndZ=0
    g21: LineSegment StartX=-16 StartY=22.5514 StartZ=0 EndX=-13.1 EndY=24.2257 EndZ=0
    g22: LineSegment StartX=-13.1 StartY=24.2257 StartZ=0 EndX=-13.1 EndY=27.5743 EndZ=0
    g23: LineSegment StartX=-13.1 StartY=27.5743 StartZ=0 EndX=-16 EndY=29.2486 EndZ=0
    g24: LineSegment StartX=-16 StartY=29.2486 StartZ=0 EndX=-18.9 EndY=27.5743 EndZ=0
    g25: Circle CenterX=-16 CenterY=25.9 CenterZ=0 NormalX=0 NormalY=0 NormalZ=1 AngleXU=0 Radius=3.34863
    g26: LineSegment StartX=13.1 StartY=27.5743 StartZ=0 EndX=13.1 EndY=24.2257 EndZ=0
    g27: LineSegment StartX=13.1 StartY=24.2257 StartZ=0 EndX=16 EndY=22.5514 EndZ=0
    g28: LineSegment StartX=16 StartY=22.5514 StartZ=0 EndX=18.9 EndY=24.2257 EndZ=0
    g29: LineSegment StartX=18.9 StartY=24.2257 StartZ=0 EndX=18.9 EndY=27.5743 EndZ=0
    g30: LineSegment StartX=18.9 StartY=27.5743 StartZ=0 EndX=16 EndY=29.2486 EndZ=0
    g31: LineSegment StartX=16 StartY=29.2486 StartZ=0 EndX=13.1 EndY=27.5743 EndZ=0
    g32: Circle CenterX=16 CenterY=25.9 CenterZ=0 NormalX=0 NormalY=0 NormalZ=1 AngleXU=0 Radius=3.34863
  constraints (78):
    c: Vertical(g0)
    c: Vertical(g1)
    c: Horizontal(g2)
    c: Coincident(g3,g-1)
    c: PointOnObject(g3,g-2)
    c: Horizontal(g4)
    c: DistanceY(g-1,g3) = 25.9
    c: DistanceY(g1,g1) = 14.2
    c: Coincident(g0,g4)
    c: Coincident(g1,g2)
    c: Coincident(g1,g4)
    c: Coincident(g0,g2)
    c: Symmetric(g0,g1,g3)
    c: Coincident(g5,g6)
    c: Coincident(g6,g7)
    c: Coincident(g7,g8)
    c: Coincident(g8,g9)
    c: Coincident(g9,g10)
    c: Coincident(g10,g5)
    c: Equal(g5, g6-g10) x5
    c: PointOnObject(g5,g11)
    c: PointOnObject(g6,g11)
    c: PointOnObject(g7,g11)
    c: PointOnObject(g8,g11)
    c: PointOnObject(g9,g11)
    c: PointOnObject(g10,g11)
    c: Coincident(g11,g0)
    c: Coincident(g12,g13)
    c: Coincident(g13,g14)
    c: Coincident(g14,g15)
    c: Coincident(g15,g16)
    c: Coincident(g16,g17)
    c: Coincident(g17,g12)
    c: Equal(g12, g13-g17) x5
    c: PointOnObject(g12,g18)
    c: PointOnObject(g13,g18)
    c: PointOnObject(g14,g18)
    c: PointOnObject(g15,g18)
    c: PointOnObject(g16,g18)
    c: PointOnObject(g17,g18)
    c: Coincident(g18,g1)
    c: Coincident(g19,g20)
    c: Coincident(g20,g21)
    c: Coincident(g21,g22)
    c: Coincident(g22,g23)
    c: Coincident(g23,g24)
    c: Coincident(g24,g19)
    c: Equal(g19, g20-g24) x5
    c: PointOnObject(g19,g25)
    c: PointOnObject(g20,g25)
    c: PointOnObject(g21,g25)
    c: PointOnObject(g22,g25)
    c: PointOnObject(g23,g25)
    c: PointOnObject(g24,g25)
    c: Coincident(g25,g0)
    c: Coincident(g26,g27)
    c: Coincident(g27,g28)
    c: Coincident(g28,g29)
    c: Coincident(g29,g30)
    c: Coincident(g30,g31)
    c: Coincident(g31,g26)
    c: Equal(g26, g27-g31) x5
    c: PointOnObject(g26,g32)
    c: PointOnObject(g27,g32)
    c: PointOnObject(g28,g32)
    c: PointOnObject(g29,g32)
    c: PointOnObject(g30,g32)
    c: PointOnObject(g31,g32)
    c: Coincident(g32,g1)
    c: Vertical(g5)
    c: Vertical(g12)
    c: Vertical(g26)
    c: Vertical(g19)
    c: Equal(g11,g25)
    c: Equal(g18,g32)
    c: DistanceX(g26,g28) = 5.8
    c: Equal(g18,g11)
    c: DistanceX(g-1,g1) = 16
FEATURE [Sketcher::SketchObject] Sketch009  label="Sketch_MCPlate"
  FullyConstrained = true
  MapMode = 5
  Support = -> [XY_Plane003]
  expr: Constraints[40] = <<params>>.mcp_side_offset_front_leng
  expr: Constraints[39] = <<params>>.mcp_cent_leng
  expr: Constraints[47] = <<params>>.mcp_tot_width / 2
  expr: Constraints[26] = <<params>>.std_rad / 2
  expr: Constraints[29] = <<params>>.std_rad
  expr: Constraints[38] = <<params>>.mcp_side_width
  expr: Constraints[86] = <<params>>.box_width + 2 * <<params>>.std_rad + 2 * <<params>>.box_wall_thick
  expr: Constraints[90] = <<params>>.bbtomcp_rear_overhang_width
  expr: Constraints[92] = <<params>>.mcp_side_offset_back_leng
  expr: Constraints[91] = <<params>>.bbtomcp_rear_overhang_leng
  sketch-geometry (38):
    g0: LineSegment StartX=56.5 StartY=38 StartZ=0 EndX=56.5 EndY=-1 EndZ=0
    g1: LineSegment StartX=54.5 StartY=-3 StartZ=0 EndX=30.5 EndY=-3 EndZ=0
    g2: LineSegment StartX=29.5 StartY=-2 StartZ=0 EndX=29.5 EndY=-1 EndZ=0
    g3: LineSegment StartX=28.5 StartY=0 StartZ=0 EndX=-28.5 EndY=0 EndZ=0
    g4: LineSegment StartX=-29.5 StartY=-1 StartZ=0 EndX=-29.5 EndY=-2 EndZ=0
    g5: LineSegment StartX=-30.5 StartY=-3 StartZ=0 EndX=-54.5 EndY=-3 EndZ=0
    g6: LineSegment StartX=-56.5 StartY=-1 StartZ=0 EndX=-56.5 EndY=38 EndZ=0
    g7: ArcOfCircle CenterX=54.5 CenterY=38 CenterZ=0 NormalX=0 NormalY=0 NormalZ=1 AngleXU=0 Radius=2 StartAngle=1e-16 EndAngle=1.57079
    g8: ArcOfCircle CenterX=54.5 CenterY=-1 CenterZ=0 NormalX=0 NormalY=0 NormalZ=1 AngleXU=0 Radius=2 StartAngle=4.71239 EndAngle=6.28319
    g9: ArcOfCircle CenterX=30.5 CenterY=-2 CenterZ=0 NormalX=0 NormalY=0 NormalZ=1 AngleXU=0 Radius=1 StartAngle=3.14159 EndAngle=4.71239
    g10: ArcOfCircle CenterX=28.5 CenterY=-1 CenterZ=0 NormalX=0 NormalY=0 NormalZ=1 AngleXU=0 Radius=1 StartAngle=0 EndAngle=1.5708
    g11: ArcOfCircle CenterX=-28.5 CenterY=-1 CenterZ=0 NormalX=0 NormalY=0 NormalZ=1 AngleXU=0 Radius=1 StartAngle=1.5708 EndAngle=3.14159
    g12: ArcOfCircle CenterX=-30.5 CenterY=-2 CenterZ=0 NormalX=0 NormalY=0 NormalZ=1 AngleXU=0 Radius=1 StartAngle=4.71239 EndAngle=6.28319
    g13: ArcOfCircle CenterX=-54.5 CenterY=-1 CenterZ=0 NormalX=0 NormalY=0 NormalZ=1 AngleXU=0 Radius=2 StartAngle=3.14159 EndAngle=4.71239
    g14: ArcOfCircle CenterX=-54.5 CenterY=38 CenterZ=0 NormalX=0 NormalY=0 NormalZ=1 AngleXU=0 Radius=2 StartAngle=1.57081 EndAngle=3.14159
    g15: LineSegment StartX=0 StartY=0 StartZ=0 EndX=0 EndY=69 EndZ=0
    g16: LineSegment StartX=56.5 StartY=38 StartZ=0 EndX=-56.5 EndY=38 EndZ=0
    g17: LineSegment StartX=-29.5 StartY=-2 StartZ=0 EndX=29.5 EndY=-2 EndZ=0
    g18: LineSegment StartX=38 StartY=40 StartZ=0 EndX=54.5 EndY=40 EndZ=0
    g19: LineSegment StartX=-54.5 StartY=40 StartZ=0 EndX=-38 EndY=40 EndZ=0
    g20: LineSegment StartX=36 StartY=42 StartZ=0 EndX=36 EndY=67 EndZ=0
    g21: LineSegment StartX=-36 StartY=67 StartZ=0 EndX=-36 EndY=42 EndZ=0
    g22: ArcOfCircle CenterX=-38 CenterY=42 CenterZ=0 NormalX=0 NormalY=0 NormalZ=1 AngleXU=0 Radius=2 StartAngle=4.71239 EndAngle=6.28319
    g23: ArcOfCircle CenterX=38 CenterY=42 CenterZ=0 NormalX=0 NormalY=0 NormalZ=1 AngleXU=0 Radius=2 StartAngle=3.14159 EndAngle=4.71239
    g24: LineSegment StartX=-34 StartY=69 StartZ=0 EndX=-15.6569 EndY=69 EndZ=0
    g25: LineSegment StartX=-14.2426 StartY=69.5858 StartZ=0 EndX=-7.41421 EndY=76.4142 EndZ=0
    g26: LineSegment StartX=-6 StartY=77 StartZ=0 EndX=6 EndY=77 EndZ=0
    g27: LineSegment StartX=7.41421 StartY=76.4142 StartZ=0 EndX=14.2426 EndY=69.5858 EndZ=0
    g28: LineSegment StartX=15.6569 StartY=69 StartZ=0 EndX=34 EndY=69 EndZ=0
    g29: ArcOfCircle CenterX=-34 CenterY=67 CenterZ=0 NormalX=0 NormalY=0 NormalZ=1 AngleXU=0 Radius=2 StartAngle=1.5708 EndAngle=3.14159
    g30: ArcOfCircle CenterX=34 CenterY=67 CenterZ=0 NormalX=0 NormalY=0 NormalZ=1 AngleXU=0 Radius=2 StartAngle=1.4e-15 EndAngle=1.5708
    g31: ArcOfCircle CenterX=15.6569 CenterY=71 CenterZ=0 NormalX=0 NormalY=0 NormalZ=1 AngleXU=0 Radius=2 StartAngle=3.92699 EndAngle=4.71239
    g32: ArcOfCircle CenterX=6 CenterY=75 CenterZ=0 NormalX=0 NormalY=0 NormalZ=1 AngleXU=0 Radius=2 StartAngle=0.785398 EndAngle=1.5708
    g33: ArcOfCircle CenterX=-6 CenterY=75 CenterZ=0 NormalX=0 NormalY=0 NormalZ=1 AngleXU=0 Radius=2 StartAngle=1.5708 EndAngle=2.35619
    g34: ArcOfCircle CenterX=-15.6569 CenterY=71 CenterZ=0 NormalX=0 NormalY=0 NormalZ=1 AngleXU=0 Radius=2 StartAngle=4.71239 EndAngle=5.49779
    g35: LineSegment StartX=-14.2426 StartY=69.5858 StartZ=0 EndX=14.2426 EndY=69.5858 EndZ=0
    g36: GeomPoint X=0 Y=77 Z=0
    g37: LineSegment StartX=-15.6569 StartY=69 StartZ=0 EndX=15.6569 EndY=69 EndZ=0
  constraints (93):
    c: Vertical(g0)
    c: Horizontal(g1)
    c: Vertical(g2)
    c: Horizontal(g3)
    c: Vertical(g4)
    c: Horizontal(g5)
    c: Vertical(g6)
    c: Tangent(g0,g7) = 1.5708
    c: Tangent(g1,g8) = 1.5708
    c: Tangent(g0,g8) = 1.5708
    c: Tangent(g1,g9) = 1.5708
    c: Tangent(g2,g9) = 1.5708
    c: Tangent(g2,g10) = -1.5708
    c: Tangent(g3,g10) = -1.5708
    c: Tangent(g3,g11) = -1.5708
    c: Tangent(g4,g11) = -1.5708
    c: Tangent(g4,g12) = 1.5708
    c: Tangent(g5,g12) = 1.5708
    c: Tangent(g5,g13) = 1.5708
    c: Tangent(g6,g13) = 1.5708
    c: Tangent(g6,g14) = 1.5708
    c: Symmetric(g3,g3,g-1)
    c: Equal(g5,g1)
    c: Equal(g10,g11)
    c: Equal(g11,g12)
    c: Equal(g12,g9)
    c: Radius(g10) = 1
    c: Equal(g8,g7)
    c: Equal(g14,g13)
    c: Radius(g8) = 2
    c: Coincident(g15,g-1)
    c: PointOnObject(g15,g-2)
    c: Coincident(g16,g0)
    c: Coincident(g16,g6)
    c: Horizontal(g16)
    c: Coincident(g17,g4)
    c: Coincident(g17,g2)
    c: Horizontal(g17)
    c: DistanceX(g2,g0) = 27
    c: DistanceY(g-1,g15) = 69
    c: DistanceY(g1,g3) = 3
    c: Horizontal(g18)
    c: Coincident(g7,g18)
    c: Tangent(g7,g18)
    c: Coincident(g19,g14)
    c: Tangent(g14,g19)
    c: Horizontal(g19)
    c: DistanceX(g-1,g0) = 56.5
    c: Vertical(g20)
    c: Vertical(g21)
    c: Equal(g13,g8)
    c: Tangent(g21,g22) = 1.5708
    c: Tangent(g19,g22) = -1.5708
    c: Tangent(g20,g23) = 1.5708
    c: Tangent(g18,g23) = -1.5708
    c: Equal(g8,g23)
    c: Equal(g23,g22)
    c: Equal(g18,g19)
    c: Horizontal(g24)
    c: Horizontal(g26)
    c: Horizontal(g28)
    c: Tangent(g21,g29) = -1.5708
    c: Tangent(g24,g29) = 1.5708
    c: Tangent(g28,g30) = 1.5708
    c: Tangent(g20,g30) = -1.5708
    c: Tangent(g28,g31) = -1.5708
    c: Tangent(g27,g31) = -1.5708
    c: Tangent(g26,g32) = 1.5708
    c: Tangent(g27,g32) = 1.5708
    c: Tangent(g26,g33) = 1.5708
    c: Tangent(g25,g33) = 1.5708
    c: Tangent(g25,g34) = -1.5708
    c: Tangent(g24,g34) = -1.5708
    c: Equal(g23,g30)
    c: Equal(g30,g31)
    c: Equal(g31,g32)
    c: Equal(g32,g33)
    c: Equal(g33,g34)
    c: Coincident(g35,g25)
    c: Coincident(g35,g27)
    c: Horizontal(g35)
    c: Angle(g27,g35) = 0.785398
    c: Angle(g35,g25) = 0.785398
    c: Equal(g22,g29)
    c: PointOnObject(g36,g-2)
    c: Symmetric(g26,g26,g36)
    c: DistanceX(g21,g20) = 72
    c: Coincident(g37,g24)
    c: Coincident(g37,g28)
    c: PointOnObject(g15,g37)
    c: DistanceX(g26,g26) = 12
    c: DistanceY(g28,g26) = 8
    c: DistanceY(g7,g28) = 29
FEATURE [PartDesign::Pad] Pad001  label="MuCPlateExt"
  Direction = (1,1,1)
  Length = 3
  Length2 = 100
  Profile = -> Sketch009
  Type = 0
  expr: Length = <<params>>.mcp_cent_thick
FEATURE [Sketcher::SketchObject] Sketch011  label="Sketch_MetroM4_MtH_Temp"
  FullyConstrained = true
  MapMode = 5
  Support = -> [XY_Plane003]
  expr: Constraints[7] = <<params>>.mm4_h3_l
  expr: Constraints[6] = <<params>>.mm4_h2_l
  expr: Constraints[4] = <<params>>.mm4_h3_w
  expr: Constraints[3] = <<params>>.mm4_h2_w
  expr: Constraints[5] = <<params>>.mm4_h4_l
  expr: Constraints[2] = <<params>>.mm4_h4_w
  expr: Constraints[1] = <<params>>.mm4_h1_l
  expr: Constraints[0] = <<params>>.mm4_h1_w
  sketch-geometry (4):
    g0: GeomPoint X=-24.13 Y=15.24 Z=0
    g1: GeomPoint X=-8.89 Y=66.04 Z=0
    g2: GeomPoint X=19.05 Y=66.04 Z=0
    g3: GeomPoint X=24.13 Y=13.97 Z=0
  constraints (8):
    c: DistanceX(g-1,g3) = 24.13
    c: DistanceY(g-1,g3) = 13.97
    c: DistanceX(g0,g-1) = 24.13
    c: DistanceX(g-1,g2) = 19.05
    c: DistanceX(g1,g-1) = 8.89
    c: DistanceY(g-1,g0) = 15.24
    c: DistanceY(g-1,g2) = 66.04
    c: DistanceY(g-1,g1) = 66.04
FEATURE [Sketcher::SketchObject] Sketch012  label="Sketch_MetroM4_MtHoles"
  FullyConstrained = true
  MapMode = 5
  Support = -> [XY_Plane003]
  expr: Constraints[15] = <<params>>.m25_hole_clear_diam
  expr: Constraints[0] = <<params>>.mm4_h1_w
  expr: Constraints[1] = <<params>>.mm4_h1_l
  expr: Constraints[2] = <<params>>.mm4_h4_w
  expr: Constraints[5] = <<params>>.mm4_h4_l
  expr: Constraints[3] = <<params>>.mm4_h2_w
  expr: Constraints[4] = <<params>>.mm4_h3_w
  expr: Constraints[6] = <<params>>.mm4_h2_l
  expr: Constraints[7] = <<params>>.mm4_h3_l
  sketch-geometry (8):
    g0: GeomPoint X=-24.13 Y=15.24 Z=0
    g1: GeomPoint X=-8.89 Y=66.04 Z=0
    g2: GeomPoint X=19.05 Y=66.04 Z=0
    g3: GeomPoint X=24.13 Y=13.97 Z=0
    g4: Circle CenterX=-8.89 CenterY=66.04 CenterZ=0 NormalX=0 NormalY=0 NormalZ=1 AngleXU=0 Radius=1.4
    g5: Circle CenterX=19.05 CenterY=66.04 CenterZ=0 NormalX=0 NormalY=0 NormalZ=1 AngleXU=0 Radius=1.4
    g6: Circle CenterX=24.13 CenterY=13.97 CenterZ=0 NormalX=0 NormalY=0 NormalZ=1 AngleXU=0 Radius=1.4
    g7: Circle CenterX=-24.13 CenterY=15.24 CenterZ=0 NormalX=0 NormalY=0 NormalZ=1 AngleXU=0 Radius=1.4
  constraints (16):
    c: DistanceX(g-1,g3) = 24.13
    c: DistanceY(g-1,g3) = 13.97
    c: DistanceX(g0,g-1) = 24.13
    c: DistanceX(g-1,g2) = 19.05
    c: DistanceX(g1,g-1) = 8.89
    c: DistanceY(g-1,g0) = 15.24
    c: DistanceY(g-1,g2) = 66.04
    c: DistanceY(g-1,g1) = 66.04
    c: Coincident(g4,g1)
    c: Coincident(g5,g2)
    c: Coincident(g6,g3)
    c: Coincident(g7,g0)
    c: Equal(g5,g4)
    c: Equal(g5,g6)
    c: Equal(g6,g7)
    c: Diameter(g6) = 2.8
FEATURE [PartDesign::Pocket] Pocket005  label="MetroM4_MtHoles"
  BaseFeature = -> Pad001
  Length = 5
  Length2 = 100
  Profile = -> Sketch012
  Reversed = true
  Type = 1
FEATURE [Sketcher::SketchObject] Sketch014  label="Sketch_MetroM4_MtCSunk"
  FullyConstrained = true
  MapMode = 5
  Support = -> [XY_Plane003]
  expr: Constraints[0] = <<params>>.mm4_h1_w
  expr: Constraints[1] = <<params>>.mm4_h1_l
  expr: Constraints[2] = <<params>>.mm4_h4_w
  expr: Constraints[5] = <<params>>.mm4_h4_l
  expr: Constraints[26] = <<params>>.m25_head_clear_diam
  expr: Constraints[3] = <<params>>.mm4_h2_w
  expr: Constraints[4] = <<params>>.mm4_h3_w
  expr: Constraints[6] = <<params>>.mm4_h2_l
  expr: Constraints[7] = <<params>>.mm4_h3_l
  sketch-geometry (14):
    g0: GeomPoint X=-24.13 Y=15.24 Z=0
    g1: GeomPoint X=-8.89 Y=66.04 Z=0
    g2: GeomPoint X=19.05 Y=66.04 Z=0
    g3: GeomPoint X=24.13 Y=13.97 Z=0
    g4: ArcOfCircle CenterX=-8.89 CenterY=66.04 CenterZ=0 NormalX=0 NormalY=0 NormalZ=1 AngleXU=0 Radius=2.5 StartAngle=3.14159 EndAngle=6.28319
    g5: ArcOfCircle CenterX=-8.89 CenterY=86.04 CenterZ=0 NormalX=0 NormalY=0 NormalZ=1 AngleXU=0 Radius=2.5 StartAngle=1.7e-15 EndAngle=3.14159
    g6: LineSegment StartX=-6.39 StartY=66.04 StartZ=0 EndX=-6.39 EndY=86.04 EndZ=0
    g7: LineSegment StartX=-11.39 StartY=66.04 StartZ=0 EndX=-11.39 EndY=86.04 EndZ=0
    g8: ArcOfCircle CenterX=19.05 CenterY=66.04 CenterZ=0 NormalX=0 NormalY=0 NormalZ=1 AngleXU=0 Radius=2.5 StartAngle=3.14159 EndAngle=6.28319
    g9: ArcOfCircle CenterX=19.05 CenterY=86.04 CenterZ=0 NormalX=0 NormalY=0 NormalZ=1 AngleXU=0 Radius=2.5 StartAngle=9e-16 EndAngle=3.14159
    g10: LineSegment StartX=21.55 StartY=66.04 StartZ=0 EndX=21.55 EndY=86.04 EndZ=0
    g11: LineSegment StartX=16.55 StartY=66.04 StartZ=0 EndX=16.55 EndY=86.04 EndZ=0
    g12: Circle CenterX=-24.13 CenterY=15.24 CenterZ=0 NormalX=0 NormalY=0 NormalZ=1 AngleXU=0 Radius=2.5
    g13: Circle CenterX=24.13 CenterY=13.97 CenterZ=0 NormalX=0 NormalY=0 NormalZ=1 AngleXU=0 Radius=2.5
  constraints (30):
    c: DistanceX(g-1,g3) = 24.13
    c: DistanceY(g-1,g3) = 13.97
    c: DistanceX(g0,g-1) = 24.13
    c: DistanceX(g-1,g2) = 19.05
    c: DistanceX(g1,g-1) = 8.89
    c: DistanceY(g-1,g0) = 15.24
    c: DistanceY(g-1,g2) = 66.04
    c: DistanceY(g-1,g1) = 66.04
    c: Tangent(g4,g7) = 1.5708
    c: Tangent(g4,g6) = -1.5708
    c: Tangent(g6,g5) = -1.5708
    c: Tangent(g7,g5) = 1.5708
    c: Vertical(g6)
    c: Equal(g4,g5)
    c: Coincident(g4,g1)
    c: Tangent(g8,g11) = 1.5708
    c: Tangent(g8,g10) = -1.5708
    c: Tangent(g10,g9) = -1.5708
    c: Tangent(g11,g9) = 1.5708
    c: Vertical(g10)
    c: Equal(g8,g9)
    c: Coincident(g8,g2)
    c: Coincident(g12,g0)
    c: Coincident(g13,g3)
    c: Equal(g4,g8)
    c: Equal(g13,g12)
    c: Diameter(g13) = 5
    c: Equal(g8,g13)
    c: Distance(g10) = 20
    c: Equal(g11,g6)
FEATURE [PartDesign::Pocket] Pocket006  label="MetroM4_CCunk"
  BaseFeature = -> Pocket005
  Length = 1.8
  Length2 = 100
  Profile = -> Sketch014
  Reversed = true
  Type = 0
  expr: Length = <<params>>.mm4_csunk_depth
FEATURE [PartDesign::Pocket] Pocket007  label="BattMtCSunk"
  BaseFeature = -> Pocket004
  Length = 1.5
  Length2 = 100
  Placement = pos=(0,0,0) rot=(1,0,0;1.5708rad)
  Profile = -> Sketch008
  Type = 0
  expr: Length = <<params>>.bat_mt_csunk_depth
FEATURE [Sketcher::SketchObject] Sketch015  label="Sketch_BattMtHexSunk001"
  FullyConstrained = true
  MapMode = 5
  Support = -> [XY_Plane003]
  expr: Constraints[91] = <<params>>.m3_nut_clear_flat
  expr: Constraints[93] = <<params>>.bat_mt_loc_w
  expr: Constraints[6] = <<params>>.bat_mt_loc_l + <<params>>.bat_mt_hexthru_loc
  expr: Constraints[7] = <<params>>.bat_mt_space
  sketch-geometry (33):
    g0: LineSegment StartX=-16 StartY=44.1 StartZ=0 EndX=-16 EndY=29.9 EndZ=0
    g1: LineSegment StartX=16 StartY=44.1 StartZ=0 EndX=16 EndY=29.9 EndZ=0
    g2: LineSegment StartX=-16 StartY=29.9 StartZ=0 EndX=16 EndY=29.9 EndZ=0
    g3: LineSegment StartX=0 StartY=0 StartZ=0 EndX=0 EndY=29.9 EndZ=0
    g4: LineSegment StartX=-16 StartY=44.1 StartZ=0 EndX=16 EndY=44.1 EndZ=0
    g5: LineSegment StartX=-18.9 StartY=45.7743 StartZ=0 EndX=-18.9 EndY=42.4257 EndZ=0
    g6: LineSegment StartX=-18.9 StartY=42.4257 StartZ=0 EndX=-16 EndY=40.7514 EndZ=0
    g7: LineSegment StartX=-16 StartY=40.7514 StartZ=0 EndX=-13.1 EndY=42.4257 EndZ=0
    g8: LineSegment StartX=-13.1 StartY=42.4257 StartZ=0 EndX=-13.1 EndY=45.7743 EndZ=0
    g9: LineSegment StartX=-13.1 StartY=45.7743 StartZ=0 EndX=-16 EndY=47.4486 EndZ=0
    g10: LineSegment StartX=-16 StartY=47.4486 StartZ=0 EndX=-18.9 EndY=45.7743 EndZ=0
    g11: Circle CenterX=-16 CenterY=44.1 CenterZ=0 NormalX=0 NormalY=0 NormalZ=1 AngleXU=0 Radius=3.34863
    g12: LineSegment StartX=13.1 StartY=45.7743 StartZ=0 EndX=13.1 EndY=42.4257 EndZ=0
    g13: LineSegment StartX=13.1 StartY=42.4257 StartZ=0 EndX=16 EndY=40.7514 EndZ=0
    g14: LineSegment StartX=16 StartY=40.7514 StartZ=0 EndX=18.9 EndY=42.4257 EndZ=0
    g15: LineSegment StartX=18.9 StartY=42.4257 StartZ=0 EndX=18.9 EndY=45.7743 EndZ=0
    g16: LineSegment StartX=18.9 StartY=45.7743 StartZ=0 EndX=16 EndY=47.4486 EndZ=0
    g17: LineSegment StartX=16 StartY=47.4486 StartZ=0 EndX=13.1 EndY=45.7743 EndZ=0
    g18: Circle CenterX=16 CenterY=44.1 CenterZ=0 NormalX=0 NormalY=0 NormalZ=1 AngleXU=0 Radius=3.34863
    g19: LineSegment StartX=-18.9 StartY=31.5743 StartZ=0 EndX=-18.9 EndY=28.2257 EndZ=0
    g20: LineSegment StartX=-18.9 StartY=28.2257 StartZ=0 EndX=-16 EndY=26.5514 EndZ=0
    g21: LineSegment StartX=-16 StartY=26.5514 StartZ=0 EndX=-13.1 EndY=28.2257 EndZ=0
    g22: LineSegment StartX=-13.1 StartY=28.2257 StartZ=0 EndX=-13.1 EndY=31.5743 EndZ=0
    g23: LineSegment StartX=-13.1 StartY=31.5743 StartZ=0 EndX=-16 EndY=33.2486 EndZ=0
    g24: LineSegment StartX=-16 StartY=33.2486 StartZ=0 EndX=-18.9 EndY=31.5743 EndZ=0
    g25: Circle CenterX=-16 CenterY=29.9 CenterZ=0 NormalX=0 NormalY=0 NormalZ=1 AngleXU=0 Radius=3.34863
    g26: LineSegment StartX=13.1 StartY=31.5743 StartZ=0 EndX=13.1 EndY=28.2257 EndZ=0
    g27: LineSegment StartX=13.1 StartY=28.2257 StartZ=0 EndX=16 EndY=26.5514 EndZ=0
    g28: LineSegment StartX=16 StartY=26.5514 StartZ=0 EndX=18.9 EndY=28.2257 EndZ=0
    g29: LineSegment StartX=18.9 StartY=28.2257 StartZ=0 EndX=18.9 EndY=31.5743 EndZ=0
    g30: LineSegment StartX=18.9 StartY=31.5743 StartZ=0 EndX=16 EndY=33.2486 EndZ=0
    g31: LineSegment StartX=16 StartY=33.2486 StartZ=0 EndX=13.1 EndY=31.5743 EndZ=0
    g32: Circle CenterX=16 CenterY=29.9 CenterZ=0 NormalX=0 NormalY=0 NormalZ=1 AngleXU=0 Radius=3.34863
  constraints (78):
    c: Vertical(g0)
    c: Vertical(g1)
    c: Horizontal(g2)
    c: Coincident(g3,g-1)
    c: PointOnObject(g3,g-2)
    c: Horizontal(g4)
    c: DistanceY(g-1,g3) = 29.9
    c: DistanceY(g1,g1) = 14.2
    c: Coincident(g0,g4)
    c: Coincident(g1,g2)
    c: Coincident(g1,g4)
    c: Coincident(g0,g2)
    c: Symmetric(g0,g1,g3)
    c: Coincident(g5,g6)
    c: Coincident(g6,g7)
    c: Coincident(g7,g8)
    c: Coincident(g8,g9)
    c: Coincident(g9,g10)
    c: Coincident(g10,g5)
    c: Equal(g5, g6-g10) x5
    c: PointOnObject(g5,g11)
    c: PointOnObject(g6,g11)
    c: PointOnObject(g7,g11)
    c: PointOnObject(g8,g11)
    c: PointOnObject(g9,g11)
    c: PointOnObject(g10,g11)
    c: Coincident(g11,g0)
    c: Coincident(g12,g13)
    c: Coincident(g13,g14)
    c: Coincident(g14,g15)
    c: Coincident(g15,g16)
    c: Coincident(g16,g17)
    c: Coincident(g17,g12)
    c: Equal(g12, g13-g17) x5
    c: PointOnObject(g12,g18)
    c: PointOnObject(g13,g18)
    c: PointOnObject(g14,g18)
    c: PointOnObject(g15,g18)
    c: PointOnObject(g16,g18)
    c: PointOnObject(g17,g18)
    c: Coincident(g18,g1)
    c: Coincident(g19,g20)
    c: Coincident(g20,g21)
    c: Coincident(g21,g22)
    c: Coincident(g22,g23)
    c: Coincident(g23,g24)
    c: Coincident(g24,g19)
    c: Equal(g19, g20-g24) x5
    c: PointOnObject(g19,g25)
    c: PointOnObject(g20,g25)
    c: PointOnObject(g21,g25)
    c: PointOnObject(g22,g25)
    c: PointOnObject(g23,g25)
    c: PointOnObject(g24,g25)
    c: Coincident(g25,g0)
    c: Coincident(g26,g27)
    c: Coincident(g27,g28)
    c: Coincident(g28,g29)
    c: Coincident(g29,g30)
    c: Coincident(g30,g31)
    c: Coincident(g31,g26)
    c: Equal(g26, g27-g31) x5
    c: PointOnObject(g26,g32)
    c: PointOnObject(g27,g32)
    c: PointOnObject(g28,g32)
    c: PointOnObject(g29,g32)
    c: PointOnObject(g30,g32)
    c: PointOnObject(g31,g32)
    c: Coincident(g32,g1)
    c: Vertical(g5)
    c: Vertical(g12)
    c: Vertical(g26)
    c: Vertical(g19)
    c: Equal(g11,g25)
    c: Equal(g18,g32)
    c: DistanceX(g26,g28) = 5.8
    c: Equal(g18,g11)
    c: DistanceX(g-1,g1) = 16
FEATURE [PartDesign::Pocket] Pocket008  label="BatMtHexThru"
  BaseFeature = -> Pocket006
  Length = 5
  Length2 = 100
  Midplane = true
  Profile = -> Sketch015
  Type = 1
FEATURE [Sketcher::SketchObject] Sketch017  label="Sketch_XiaoMt_Holes"
  FullyConstrained = true
  MapMode = 5
  Support = -> [XY_Plane003]
  expr: Constraints[36] = <<params>>.m2_hole_clear_diam
  expr: Constraints[24] = <<params>>.mcp_xiaomt_width
  expr: Constraints[25] = <<params>>.mcp_xiaomt_leng
  expr: Constraints[40] = <<params>>.mcp_tot_width - 2 * <<params>>.mcp_xiaomt_edgeclear_w
  expr: Constraints[41] = <<params>>.mcp_side_offset_front_leng - <<params>>.mcp_xiaomt_edgeclear_l
  sketch-geometry (17):
    g0: LineSegment StartX=33 StartY=36 StartZ=0 EndX=53 EndY=36 EndZ=0
    g1: LineSegment StartX=53 StartY=36 StartZ=0 EndX=53 EndY=1 EndZ=0
    g2: LineSegment StartX=53 StartY=1 StartZ=0 EndX=33 EndY=1 EndZ=0
    g3: LineSegment StartX=33 StartY=1 StartZ=0 EndX=33 EndY=36 EndZ=0
    g4: LineSegment StartX=-53 StartY=36 StartZ=0 EndX=-33 EndY=36 EndZ=0
    g5: LineSegment StartX=-33 StartY=36 StartZ=0 EndX=-33 EndY=1 EndZ=0
    g6: LineSegment StartX=-33 StartY=1 StartZ=0 EndX=-53 EndY=1 EndZ=0
    g7: LineSegment StartX=-53 StartY=1 StartZ=0 EndX=-53 EndY=36 EndZ=0
    g8: LineSegment StartX=-33 StartY=1 StartZ=0 EndX=33 EndY=1 EndZ=0
    g9: LineSegment StartX=-33 StartY=36 StartZ=0 EndX=33 EndY=36 EndZ=0
    g10: LineSegment StartX=0 StartY=0 StartZ=0 EndX=0 EndY=1 EndZ=0
    g11: Circle CenterX=-53 CenterY=36 CenterZ=0 NormalX=0 NormalY=0 NormalZ=1 AngleXU=0 Radius=1.15
    g12: Circle CenterX=-33 CenterY=1 CenterZ=0 NormalX=0 NormalY=0 NormalZ=1 AngleXU=0 Radius=1.15
    g13: Circle CenterX=-53 CenterY=1 CenterZ=0 NormalX=0 NormalY=0 NormalZ=1 AngleXU=0 Radius=1.15
    g14: Circle CenterX=53 CenterY=36 CenterZ=0 NormalX=0 NormalY=0 NormalZ=1 AngleXU=0 Radius=1.15
    g15: Circle CenterX=53 CenterY=1 CenterZ=0 NormalX=0 NormalY=0 NormalZ=1 AngleXU=0 Radius=1.15
    g16: Circle CenterX=33 CenterY=1 CenterZ=0 NormalX=0 NormalY=0 NormalZ=1 AngleXU=0 Radius=1.15
  constraints (42):
    c: Coincident(g0,g1)
    c: Coincident(g1,g2)
    c: Coincident(g2,g3)
    c: Coincident(g3,g0)
    c: Horizontal(g0)
    c: Horizontal(g2)
    c: Vertical(g1)
    c: Vertical(g3)
    c: Coincident(g4,g5)
    c: Coincident(g5,g6)
    c: Coincident(g6,g7)
    c: Coincident(g7,g4)
    c: Horizontal(g4)
    c: Horizontal(g6)
    c: Vertical(g5)
    c: Vertical(g7)
    c: Coincident(g8,g5)
    c: Coincident(g8,g2)
    c: Horizontal(g8)
    c: Coincident(g9,g4)
    c: Coincident(g9,g0)
    c: Symmetric(g5,g2,g10)
    c: Horizontal(g9)
    c: Equal(g0,g4)
    c: DistanceX(g0,g0) = 20
    c: DistanceY(g1,g0) = 35
    c: Coincident(g11,g4)
    c: Coincident(g12,g5)
    c: Coincident(g13,g6)
    c: Coincident(g14,g0)
    c: Coincident(g15,g1)
    c: Coincident(g16,g2)
    c: Equal(g14,g15)
    c: Equal(g15,g16)
    c: Equal(g16,g12)
    c: Equal(g11,g13)
    c: Diameter(g14) = 2.3
    c: Equal(g12,g13)
    c: Vertical(g10)
    c: Coincident(g10,g-1)
    c: DistanceX(g13,g15) = 106
    c: DistanceY(g16,g-1) = -1
FEATURE [PartDesign::Pocket] Pocket009  label="XiaoMtHoles"
  BaseFeature = -> Pocket008
  Length = 5
  Length2 = 100
  Midplane = true
  Profile = -> Sketch017
  Type = 1
FEATURE [Sketcher::SketchObject] Sketch018  label="Sketch_XiaoMt_HexSunk"
  FullyConstrained = true
  MapMode = 5
  Support = -> [XY_Plane003]
  expr: Constraints[29] = <<params>>.mcp_xiaomt_width
  expr: Constraints[152] = <<params>>.mcp_side_offset_front_leng - <<params>>.mcp_xiaomt_edgeclear_l
  expr: Constraints[30] = <<params>>.mcp_xiaomt_leng
  expr: Constraints[150] = <<params>>.m2_nut_clear_flat
  expr: Constraints[2] = <<params>>.mcp_cent_leng
  expr: Constraints[151] = <<params>>.mcp_tot_width - 2 * <<params>>.mcp_xiaomt_edgeclear_w
  sketch-geometry (54):
    g0: LineSegment StartX=0 StartY=0 StartZ=0 EndX=0 EndY=69 EndZ=0
    g1: LineSegment StartX=33 StartY=36 StartZ=0 EndX=53 EndY=36 EndZ=0
    g2: LineSegment StartX=53 StartY=36 StartZ=0 EndX=53 EndY=1 EndZ=0
    g3: LineSegment StartX=53 StartY=1 StartZ=0 EndX=33 EndY=1 EndZ=0
    g4: LineSegment StartX=33 StartY=1 StartZ=0 EndX=33 EndY=36 EndZ=0
    g5: LineSegment StartX=-53 StartY=36 StartZ=0 EndX=-33 EndY=36 EndZ=0
    g6: LineSegment StartX=-33 StartY=36 StartZ=0 EndX=-33 EndY=1 EndZ=0
    g7: LineSegment StartX=-33 StartY=1 StartZ=0 EndX=-53 EndY=1 EndZ=0
    g8: LineSegment StartX=-53 StartY=1 StartZ=0 EndX=-53 EndY=36 EndZ=0
    g9: LineSegment StartX=-33 StartY=1 StartZ=0 EndX=33 EndY=1 EndZ=0
    g10: LineSegment StartX=-33 StartY=36 StartZ=0 EndX=33 EndY=36 EndZ=0
    g11: LineSegment StartX=0 StartY=0 StartZ=0 EndX=0 EndY=1 EndZ=0
    g12: LineSegment StartX=53 StartY=33.5751 StartZ=0 EndX=55.1 EndY=34.7876 EndZ=0
    g13: LineSegment StartX=55.1 StartY=34.7876 StartZ=0 EndX=55.1 EndY=37.2124 EndZ=0
    g14: LineSegment StartX=55.1 StartY=37.2124 StartZ=0 EndX=53 EndY=38.4249 EndZ=0
    g15: LineSegment StartX=53 StartY=38.4249 StartZ=0 EndX=50.9 EndY=37.2124 EndZ=0
    g16: LineSegment StartX=50.9 StartY=37.2124 StartZ=0 EndX=50.9 EndY=34.7876 EndZ=0
    g17: LineSegment StartX=50.9 StartY=34.7876 StartZ=0 EndX=53 EndY=33.5751 EndZ=0
    g18: Circle CenterX=53 CenterY=36 CenterZ=0 NormalX=0 NormalY=0 NormalZ=1 AngleXU=0 Radius=2.42487
    g19: LineSegment StartX=53 StartY=3.42487 StartZ=0 EndX=50.9 EndY=2.21244 EndZ=0
    g20: LineSegment StartX=50.9 StartY=2.21244 StartZ=0 EndX=50.9 EndY=-0.212436 EndZ=0
    g21: LineSegment StartX=50.9 StartY=-0.212436 StartZ=0 EndX=53 EndY=-1.42487 EndZ=0
    g22: LineSegment StartX=53 StartY=-1.42487 StartZ=0 EndX=55.1 EndY=-0.212436 EndZ=0
    g23: LineSegment StartX=55.1 StartY=-0.212436 StartZ=0 EndX=55.1 EndY=2.21244 EndZ=0
    g24: LineSegment StartX=55.1 StartY=2.21244 StartZ=0 EndX=53 EndY=3.42487 EndZ=0
    g25: Circle CenterX=53 CenterY=1 CenterZ=0 NormalX=0 NormalY=0 NormalZ=1 AngleXU=0 Radius=2.42487
    g26: LineSegment StartX=33 StartY=3.42487 StartZ=0 EndX=30.9 EndY=2.21244 EndZ=0
    g27: LineSegment StartX=30.9 StartY=2.21244 StartZ=0 EndX=30.9 EndY=-0.212436 EndZ=0
    g28: LineSegment StartX=30.9 StartY=-0.212436 StartZ=0 EndX=33 EndY=-1.42487 EndZ=0
    g29: LineSegment StartX=33 StartY=-1.42487 StartZ=0 EndX=35.1 EndY=-0.212436 EndZ=0
    g30: LineSegment StartX=35.1 StartY=-0.212436 StartZ=0 EndX=35.1 EndY=2.21244 EndZ=0
    g31: LineSegment StartX=35.1 StartY=2.21244 StartZ=0 EndX=33 EndY=3.42487 EndZ=0
    g32: Circle CenterX=33 CenterY=1 CenterZ=0 NormalX=0 NormalY=0 NormalZ=1 AngleXU=0 Radius=2.42487
    g33: LineSegment StartX=-33 StartY=3.42487 StartZ=0 EndX=-35.1 EndY=2.21244 EndZ=0
    g34: LineSegment StartX=-35.1 StartY=2.21244 StartZ=0 EndX=-35.1 EndY=-0.212436 EndZ=0
    g35: LineSegment StartX=-35.1 StartY=-0.212436 StartZ=0 EndX=-33 EndY=-1.42487 EndZ=0
    g36: LineSegment StartX=-33 StartY=-1.42487 StartZ=0 EndX=-30.9 EndY=-0.212436 EndZ=0
    g37: LineSegment StartX=-30.9 StartY=-0.212436 StartZ=0 EndX=-30.9 EndY=2.21244 EndZ=0
    g38: LineSegment StartX=-30.9 StartY=2.21244 StartZ=0 EndX=-33 EndY=3.42487 EndZ=0
    g39: Circle CenterX=-33 CenterY=1 CenterZ=0 NormalX=0 NormalY=0 NormalZ=1 AngleXU=0 Radius=2.42487
    g40: LineSegment StartX=-53 StartY=3.42487 StartZ=0 EndX=-55.1 EndY=2.21244 EndZ=0
    g41: LineSegment StartX=-55.1 StartY=2.21244 StartZ=0 EndX=-55.1 EndY=-0.212436 EndZ=0
    g42: LineSegment StartX=-55.1 StartY=-0.212436 StartZ=0 EndX=-53 EndY=-1.42487 EndZ=0
    g43: LineSegment StartX=-53 StartY=-1.42487 StartZ=0 EndX=-50.9 EndY=-0.212436 EndZ=0
    g44: LineSegment StartX=-50.9 StartY=-0.212436 StartZ=0 EndX=-50.9 EndY=2.21244 EndZ=0
    g45: LineSegment StartX=-50.9 StartY=2.21244 StartZ=0 EndX=-53 EndY=3.42487 EndZ=0
    g46: Circle CenterX=-53 CenterY=1 CenterZ=0 NormalX=0 NormalY=0 NormalZ=1 AngleXU=0 Radius=2.42487
    g47: LineSegment StartX=-53 StartY=33.5751 StartZ=0 EndX=-50.9 EndY=34.7876 EndZ=0
    g48: LineSegment StartX=-50.9 StartY=34.7876 StartZ=0 EndX=-50.9 EndY=37.2124 EndZ=0
    g49: LineSegment StartX=-50.9 StartY=37.2124 StartZ=0 EndX=-53 EndY=38.4249 EndZ=0
    g50: LineSegment StartX=-53 StartY=38.4249 StartZ=0 EndX=-55.1 EndY=37.2124 EndZ=0
    g51: LineSegment StartX=-55.1 StartY=37.2124 StartZ=0 EndX=-55.1 EndY=34.7876 EndZ=0
    g52: LineSegment StartX=-55.1 StartY=34.7876 StartZ=0 EndX=-53 EndY=33.5751 EndZ=0
    g53: Circle CenterX=-53 CenterY=36 CenterZ=0 NormalX=0 NormalY=0 NormalZ=1 AngleXU=0 Radius=2.42487
  constraints (129):
    c: Coincident(g0,g-1)
    c: PointOnObject(g0,g-2)
    c: DistanceY(g-1,g0) = 69
    c: Coincident(g1,g2)
    c: Coincident(g2,g3)
    c: Coincident(g3,g4)
    c: Coincident(g4,g1)
    c: Horizontal(g1)
    c: Horizontal(g3)
    c: Vertical(g2)
    c: Vertical(g4)
    c: Coincident(g5,g6)
    c: Coincident(g6,g7)
    c: Coincident(g7,g8)
    c: Coincident(g8,g5)
    c: Horizontal(g5)
    c: Horizontal(g7)
    c: Vertical(g6)
    c: Vertical(g8)
    c: Coincident(g9,g6)
    c: Coincident(g9,g3)
    c: Horizontal(g9)
    c: Coincident(g10,g5)
    c: Coincident(g10,g1)
    c: Coincident(g11,g0)
    c: PointOnObject(g11,g0)
    c: Symmetric(g6,g3,g11)
    c: Horizontal(g10)
    c: Equal(g1,g5)
    c: DistanceX(g1,g1) = 20
    c: DistanceY(g2,g1) = 35
    c: Coincident(g12,g13)
    c: Coincident(g13,g14)
    c: Coincident(g14,g15)
    c: Coincident(g15,g16)
    c: Coincident(g16,g17)
    c: Coincident(g17,g12)
    c: Equal(g12, g13-g17) x5
    c: PointOnObject(g12,g18)
    c: PointOnObject(g13,g18)
    c: PointOnObject(g14,g18)
    c: PointOnObject(g15,g18)
    c: PointOnObject(g16,g18)
    c: PointOnObject(g17,g18)
    c: Coincident(g18,g1)
    c: PointOnObject(g17,g2)
    c: Coincident(g19,g20)
    c: Coincident(g20,g21)
    c: Coincident(g21,g22)
    c: Coincident(g22,g23)
    c: Coincident(g23,g24)
    c: Coincident(g24,g19)
    c: Equal(g19, g20-g24) x5
    c: PointOnObject(g19,g25)
    c: PointOnObject(g20,g25)
    c: PointOnObject(g21,g25)
    c: PointOnObject(g22,g25)
    c: PointOnObject(g23,g25)
    c: PointOnObject(g24,g25)
    c: Coincident(g25,g2)
    c: PointOnObject(g24,g2)
    c: Coincident(g26,g27)
    c: Coincident(g27,g28)
    c: Coincident(g28,g29)
    c: Coincident(g29,g30)
    c: Coincident(g30,g31)
    c: Coincident(g31,g26)
    c: Equal(g26, g27-g31) x5
    c: PointOnObject(g26,g32)
    c: PointOnObject(g27,g32)
    c: PointOnObject(g28,g32)
    c: PointOnObject(g29,g32)
    c: PointOnObject(g30,g32)
    c: PointOnObject(g31,g32)
    c: Coincident(g32,g3)
    c: Coincident(g33,g34)
    c: Coincident(g34,g35)
    c: Coincident(g35,g36)
    c: Coincident(g36,g37)
    c: Coincident(g37,g38)
    c: Coincident(g38,g33)
    c: Equal(g33, g34-g38) x5
    c: PointOnObject(g33,g39)
    c: PointOnObject(g34,g39)
    c: PointOnObject(g35,g39)
    c: PointOnObject(g36,g39)
    c: PointOnObject(g37,g39)
    c: PointOnObject(g38,g39)
    c: Coincident(g39,g6)
    c: PointOnObject(g38,g6)
    c: Coincident(g40,g41)
    c: Coincident(g41,g42)
    c: Coincident(g42,g43)
    c: Coincident(g43,g44)
    c: Coincident(g44,g45)
    c: Coincident(g45,g40)
    c: Equal(g40, g41-g45) x5
    c: PointOnObject(g40,g46)
    c: PointOnObject(g41,g46)
    c: PointOnObject(g42,g46)
    c: PointOnObject(g43,g46)
    c: PointOnObject(g44,g46)
    c: PointOnObject(g45,g46)
    c: Coincident(g46,g7)
    c: PointOnObject(g45,g8)
    c: Coincident(g47,g48)
    c: Coincident(g48,g49)
    c: Coincident(g49,g50)
    c: Coincident(g50,g51)
    c: Coincident(g51,g52)
    c: Coincident(g52,g47)
    c: Equal(g47, g48-g52) x5
    c: PointOnObject(g47,g53)
    c: PointOnObject(g48,g53)
    c: PointOnObject(g49,g53)
    c: PointOnObject(g50,g53)
    c: PointOnObject(g51,g53)
    c: PointOnObject(g52,g53)
    c: Coincident(g53,g5)
    c: PointOnObject(g52,g8)
    c: Equal(g53,g46)
    c: Equal(g46,g39)
    c: Equal(g39,g32)
    c: Vertical(g27)
    c: Equal(g32,g25)
    c: Equal(g25,g18)
    c: DistanceX(g20,g22) = 4.2
    c: DistanceX(g7,g2) = 106
    c: DistanceY(g11,g0) = -1
FEATURE [PartDesign::Pocket] Pocket010  label="XiaoMtHexSunk"
  BaseFeature = -> Pocket009
  Length = 1.8
  Length2 = 100
  Profile = -> Sketch018
  Reversed = true
  Type = 0
  expr: Length = <<params>>.m2_nut_min_depth
FEATURE [PartDesign::Plane] DatumPlane003  label="Datum_BattBoxTop"
  AttachmentOffset = pos=(0,0,17) rot=(0,0,1;0rad)
  Length = 106.573
  MapMode = 5
  Placement = pos=(0,0,17) rot=(0,0,1;0rad)
  ResizeMode = 0
  Support = -> [XY_Plane001]
  Width = 116.573
  expr: .AttachmentOffset.Base.z = <<params>>.box_height_tot
FEATURE [Sketcher::SketchObject] Sketch020  label="Sketch_BattBToMCP_HoleLocTemp"
  FullyConstrained = true
  MapMode = 5
  Placement = pos=(0,0,17) rot=(0,0,1;0rad)
  Support = -> [DatumPlane003]
  expr: Constraints[5] = Spreadsheet.bbtomcp_hole_space_width
  expr: Constraints[4] = <<params>>.bbtomcp_hole_loc_leng
  sketch-geometry (2):
    g0: LineSegment StartX=0 StartY=0 StartZ=0 EndX=0 EndY=5 EndZ=0
    g1: LineSegment StartX=-40 StartY=5 StartZ=0 EndX=40 EndY=5 EndZ=0
  constraints (6):
    c: Coincident(g0,g-1)
    c: PointOnObject(g0,g-2)
    c: Horizontal(g1)
    c: Symmetric(g1,g1,g0)
    c: DistanceY(g-1,g1) = 5
    c: DistanceX(g1,g1) = 80
FEATURE [Sketcher::SketchObject] Sketch021  label="Sketch_BattBToMCP_HoleLoc"
  FullyConstrained = true
  MapMode = 5
  Placement = pos=(0,0,17) rot=(0,0,1;0rad)
  Support = -> [DatumPlane003]
  expr: Constraints[4] = <<params>>.m2_hole_clear_diam
  expr: Constraints[14] = <<params>>.box_mt_offset_leng
  expr: Constraints[22] = <<params>>.bbtomcp_hole_space_leng - <<params>>.bbtomcp_rear_hole_offset_leng
  expr: Constraints[16] = <<params>>.bbtomcp_rear_hole_spacing_width
  expr: Constraints[15] = <<params>>.bbtomcp_hole_space_width
  sketch-geometry (10):
    g0: LineSegment StartX=0 StartY=0 StartZ=0 EndX=0 EndY=68.5 EndZ=0
    g1: Circle CenterX=-2.7 CenterY=68.5 CenterZ=0 NormalX=0 NormalY=0 NormalZ=1 AngleXU=0 Radius=1.15
    g2: Circle CenterX=2.7 CenterY=68.5 CenterZ=0 NormalX=0 NormalY=0 NormalZ=1 AngleXU=0 Radius=1.15
    g3: LineSegment StartX=-2.7 StartY=68.5 StartZ=0 EndX=-40 EndY=5 EndZ=0
    g4: LineSegment StartX=2.7 StartY=68.5 StartZ=0 EndX=40 EndY=5 EndZ=0
    g5: LineSegment StartX=-40 StartY=5 StartZ=0 EndX=40 EndY=5 EndZ=0
    g6: Circle CenterX=-40 CenterY=5 CenterZ=0 NormalX=0 NormalY=0 NormalZ=1 AngleXU=0 Radius=1.15
    g7: Circle CenterX=40 CenterY=5 CenterZ=0 NormalX=0 NormalY=0 NormalZ=1 AngleXU=0 Radius=1.15
    g8: LineSegment StartX=-2.7 StartY=68.5 StartZ=0 EndX=2.7 EndY=68.5 EndZ=0
    g9: GeomPoint X=0 Y=5 Z=0
  constraints (23):
    c: Coincident(g0,g-1)
    c: PointOnObject(g0,g-2)
    c: Symmetric(g1,g2,g0)
    c: Equal(g1,g2)
    c: Diameter(g2) = 2.3
    c: Coincident(g3,g1)
    c: Coincident(g4,g2)
    c: Coincident(g5,g3)
    c: Coincident(g5,g4)
    c: Horizontal(g5)
    c: Coincident(g6,g3)
    c: Coincident(g7,g4)
    c: Equal(g2,g7)
    c: Equal(g7,g6)
    c: DistanceY(g-1,g7) = 5
    c: DistanceX(g6,g7) = 80
    c: DistanceX(g1,g2) = 5.4
    c: Coincident(g8,g1)
    c: Coincident(g8,g2)
    c: Horizontal(g8)
    c: PointOnObject(g9,g0)
    c: Symmetric(g6,g7,g9)
    c: DistanceY(g-1,g2) = 68.5
FEATURE [PartDesign::Pocket] Pocket012  label="BBToMCP_MtHoles"
  BaseFeature = -> Pocket007
  Length = 5.7
  Length2 = 100
  Placement = pos=(0,0,0) rot=(1,0,0;1.5708rad)
  Profile = -> Sketch021
  Type = 0
  expr: Length = <<params>>.bbtomcp_tot_height
FEATURE [Sketcher::SketchObject] Sketch022  label="Sketch_BattBToMCP_HoleLocTemp001"
  FullyConstrained = true
  MapMode = 5
  Support = -> [XY_Plane003]
  expr: Constraints[4] = <<params>>.bbtomcp_hole_loc_leng + <<params>>.mcp_cent_overhang
  expr: Constraints[5] = Spreadsheet.bbtomcp_hole_space_width
  sketch-geometry (2):
    g0: LineSegment StartX=0 StartY=0 StartZ=0 EndX=0 EndY=9 EndZ=0
    g1: LineSegment StartX=-40 StartY=9 StartZ=0 EndX=40 EndY=9 EndZ=0
  constraints (6):
    c: Coincident(g0,g-1)
    c: PointOnObject(g0,g-2)
    c: Horizontal(g1)
    c: Symmetric(g1,g1,g0)
    c: DistanceY(g-1,g1) = 9
    c: DistanceX(g1,g1) = 80
FEATURE [Sketcher::SketchObject] Sketch023  label="Sketch_BattBToMCP_Holes"
  FullyConstrained = true
  MapMode = 5
  Support = -> [XY_Plane003]
  expr: Constraints[22] = <<params>>.bbtomcp_hole_space_leng - <<params>>.bbtomcp_rear_hole_offset_leng + <<params>>.bbtomcp_leng_diff
  expr: Constraints[21] = <<params>>.bbtomcp_rear_hole_spacing_width
  expr: Constraints[5] = Spreadsheet.bbtomcp_hole_space_width
  expr: Constraints[4] = <<params>>.bbtomcp_hole_loc_leng + <<params>>.mcp_cent_overhang
  expr: Constraints[8] = <<params>>.m2_hole_clear_diam
  sketch-geometry (10):
    g0: LineSegment StartX=0 StartY=0 StartZ=0 EndX=0 EndY=9 EndZ=0
    g1: LineSegment StartX=-40 StartY=9 StartZ=0 EndX=40 EndY=9 EndZ=0
    g2: Circle CenterX=-40 CenterY=9 CenterZ=0 NormalX=0 NormalY=0 NormalZ=1 AngleXU=0 Radius=1.15
    g3: Circle CenterX=40 CenterY=9 CenterZ=0 NormalX=0 NormalY=0 NormalZ=1 AngleXU=0 Radius=1.15
    g4: LineSegment StartX=-40 StartY=9 StartZ=0 EndX=-2.7 EndY=72.5 EndZ=0
    g5: LineSegment StartX=40 StartY=9 StartZ=0 EndX=2.7 EndY=72.5 EndZ=0
    g6: LineSegment StartX=-2.7 StartY=72.5 StartZ=0 EndX=2.7 EndY=72.5 EndZ=0
    g7: Circle CenterX=2.7 CenterY=72.5 CenterZ=0 NormalX=0 NormalY=0 NormalZ=1 AngleXU=0 Radius=1.15
    g8: Circle CenterX=-2.7 CenterY=72.5 CenterZ=0 NormalX=0 NormalY=0 NormalZ=1 AngleXU=0 Radius=1.15
    g9: GeomPoint X=0 Y=72.5 Z=0
  constraints (23):
    c: Coincident(g0,g-1)
    c: PointOnObject(g0,g-2)
    c: Horizontal(g1)
    c: Symmetric(g1,g1,g0)
    c: DistanceY(g-1,g1) = 9
    c: DistanceX(g1,g1) = 80
    c: Coincident(g2,g1)
    c: Coincident(g3,g1)
    c: Diameter(g3) = 2.3
    c: Equal(g3,g2)
    c: Coincident(g4,g2)
    c: Coincident(g5,g3)
    c: Coincident(g6,g4)
    c: Coincident(g6,g5)
    c: Horizontal(g6)
    c: Coincident(g7,g5)
    c: Coincident(g8,g4)
    c: Equal(g3,g7)
    c: Equal(g7,g8)
    c: PointOnObject(g9,g-2)
    c: Symmetric(g8,g7,g9)
    c: DistanceX(g8,g7) = 5.4
    c: DistanceY(g-1,g7) = 72.5
FEATURE [PartDesign::Pocket] Pocket013  label="BBToMcp_MtHoles"
  BaseFeature = -> Pocket010
  Length = 5
  Length2 = 100
  Midplane = true
  Profile = -> Sketch023
  Type = 1
FEATURE [PartDesign::Plane] DatumPlane004  label="Datum_TopMtHexSlot"
  AttachmentOffset = pos=(0,0,15.4) rot=(0,0,1;0rad)
  Length = 106.573
  MapMode = 5
  Placement = pos=(0,0,15.4) rot=(0,0,1;0rad)
  ResizeMode = 0
  Support = -> [XY_Plane001]
  Width = 116.573
  expr: .AttachmentOffset.Base.z = <<params>>.bbtomcp_hex_slot_z
FEATURE [PartDesign::Plane] DatumPlane005  label="Datum_TopMtHexSunk"
  AttachmentOffset = pos=(0,0,13.1) rot=(0,0,1;0rad)
  Length = 106.573
  MapMode = 5
  Placement = pos=(0,0,13.1) rot=(0,0,1;0rad)
  ResizeMode = 0
  Support = -> [XY_Plane001]
  Width = 116.573
  expr: .AttachmentOffset.Base.z = <<params>>.bbtomcp_hex_sunk_z
FEATURE [Sketcher::SketchObject] Sketch024  label="Sketch_BattBToMCP_HexSunk"
  FullyConstrained = true
  MapMode = 5
  Placement = pos=(0,0,13.1) rot=(0,0,1;0rad)
  Support = -> [DatumPlane005]
  expr: Constraints[75] = <<params>>.bbtomcp_hole_loc_leng
  expr: Constraints[79] = <<params>>.m2_nut_clear_flat
  expr: Constraints[90] = <<params>>.bbtomcp_hole_space_leng - <<params>>.bbtomcp_rear_hole_offset_leng
  expr: Constraints[80] = <<params>>.bbtomcp_hole_space_width
  expr: Constraints[81] = <<params>>.bbtomcp_rear_hole_spacing_width
  sketch-geometry (32):
    g0: LineSegment StartX=0 StartY=0 StartZ=0 EndX=0 EndY=68.5 EndZ=0
    g1: LineSegment StartX=-2.7 StartY=68.5 StartZ=0 EndX=2.7 EndY=68.5 EndZ=0
    g2: LineSegment StartX=-40 StartY=5 StartZ=0 EndX=40 EndY=5 EndZ=0
    g3: LineSegment StartX=0.6 StartY=67.2876 StartZ=0 EndX=2.7 EndY=66.0751 EndZ=0
    g4: LineSegment StartX=2.7 StartY=66.0751 StartZ=0 EndX=4.8 EndY=67.2876 EndZ=0
    g5: LineSegment StartX=4.8 StartY=67.2876 StartZ=0 EndX=4.8 EndY=69.7124 EndZ=0
    g6: LineSegment StartX=4.8 StartY=69.7124 StartZ=0 EndX=2.7 EndY=70.9249 EndZ=0
    g7: LineSegment StartX=2.7 StartY=70.9249 StartZ=0 EndX=0.6 EndY=69.7124 EndZ=0
    g8: LineSegment StartX=0.6 StartY=69.7124 StartZ=0 EndX=0.6 EndY=67.2876 EndZ=0
    g9: Circle CenterX=2.7 CenterY=68.5 CenterZ=0 NormalX=0 NormalY=0 NormalZ=1 AngleXU=0 Radius=2.42487
    g10: LineSegment StartX=40 StartY=7.42487 StartZ=0 EndX=37.9 EndY=6.21244 EndZ=0
    g11: LineSegment StartX=37.9 StartY=6.21244 StartZ=0 EndX=37.9 EndY=3.78756 EndZ=0
    g12: LineSegment StartX=37.9 StartY=3.78756 StartZ=0 EndX=40 EndY=2.57513 EndZ=0
    g13: LineSegment StartX=40 StartY=2.57513 StartZ=0 EndX=42.1 EndY=3.78756 EndZ=0
    g14: LineSegment StartX=42.1 StartY=3.78756 StartZ=0 EndX=42.1 EndY=6.21244 EndZ=0
    g15: LineSegment StartX=42.1 StartY=6.21244 StartZ=0 EndX=40 EndY=7.42487 EndZ=0
    g16: Circle CenterX=40 CenterY=5 CenterZ=0 NormalX=0 NormalY=0 NormalZ=1 AngleXU=0 Radius=2.42487
    g17: LineSegment StartX=-37.9 StartY=6.21244 StartZ=0 EndX=-40 EndY=7.42487 EndZ=0
    g18: LineSegment StartX=-40 StartY=7.42487 StartZ=0 EndX=-42.1 EndY=6.21244 EndZ=0
    g19: LineSegment StartX=-42.1 StartY=6.21244 StartZ=0 EndX=-42.1 EndY=3.78756 EndZ=0
    g20: LineSegment StartX=-42.1 StartY=3.78756 StartZ=0 EndX=-40 EndY=2.57513 EndZ=0
    g21: LineSegment StartX=-40 StartY=2.57513 StartZ=0 EndX=-37.9 EndY=3.78756 EndZ=0
    g22: LineSegment StartX=-37.9 StartY=3.78756 StartZ=0 EndX=-37.9 EndY=6.21244 EndZ=0
    g23: Circle CenterX=-40 CenterY=5 CenterZ=0 NormalX=0 NormalY=0 NormalZ=1 AngleXU=0 Radius=2.42487
    g24: LineSegment StartX=-4.8 StartY=67.2876 StartZ=0 EndX=-2.7 EndY=66.0751 EndZ=0
    g25: LineSegment StartX=-2.7 StartY=66.0751 StartZ=0 EndX=-0.6 EndY=67.2876 EndZ=0
    g26: LineSegment StartX=-0.6 StartY=67.2876 StartZ=0 EndX=-0.6 EndY=69.7124 EndZ=0
    g27: LineSegment StartX=-0.6 StartY=69.7124 StartZ=0 EndX=-2.7 EndY=70.9249 EndZ=0
    g28: LineSegment StartX=-2.7 StartY=70.9249 StartZ=0 EndX=-4.8 EndY=69.7124 EndZ=0
    g29: LineSegment StartX=-4.8 StartY=69.7124 StartZ=0 EndX=-4.8 EndY=67.2876 EndZ=0
    g30: Circle CenterX=-2.7 CenterY=68.5 CenterZ=0 NormalX=0 NormalY=0 NormalZ=1 AngleXU=0 Radius=2.42487
    g31: GeomPoint X=0 Y=5 Z=0
  constraints (75):
    c: Coincident(g0,g-1)
    c: PointOnObject(g0,g-2)
    c: Horizontal(g1)
    c: Symmetric(g1,g1,g0)
    c: Coincident(g3,g4)
    c: Coincident(g4,g5)
    c: Coincident(g5,g6)
    c: Coincident(g6,g7)
    c: Coincident(g7,g8)
    c: Coincident(g8,g3)
    c: Equal(g3, g4-g8) x5
    c: PointOnObject(g3,g9)
    c: PointOnObject(g4,g9)
    c: PointOnObject(g5,g9)
    c: PointOnObject(g6,g9)
    c: PointOnObject(g7,g9)
    c: PointOnObject(g8,g9)
    c: Coincident(g9,g1)
    c: Coincident(g10,g11)
    c: Coincident(g11,g12)
    c: Coincident(g12,g13)
    c: Coincident(g13,g14)
    c: Coincident(g14,g15)
    c: Coincident(g15,g10)
    c: Equal(g10, g11-g15) x5
    c: PointOnObject(g10,g16)
    c: PointOnObject(g11,g16)
    c: PointOnObject(g12,g16)
    c: PointOnObject(g13,g16)
    c: PointOnObject(g14,g16)
    c: PointOnObject(g15,g16)
    c: Coincident(g17,g18)
    c: Coincident(g18,g19)
    c: Coincident(g19,g20)
    c: Coincident(g20,g21)
    c: Coincident(g21,g22)
    c: Coincident(g22,g17)
    c: Equal(g17, g18-g22) x5
    c: PointOnObject(g17,g23)
    c: PointOnObject(g18,g23)
    c: PointOnObject(g19,g23)
    c: PointOnObject(g20,g23)
    c: PointOnObject(g21,g23)
    c: PointOnObject(g22,g23)
    c: Coincident(g24,g25)
    c: Coincident(g25,g26)
    c: Coincident(g26,g27)
    c: Coincident(g27,g28)
    c: Coincident(g28,g29)
    c: Coincident(g29,g24)
    c: Equal(g24, g25-g29) x5
    c: PointOnObject(g24,g30)
    c: PointOnObject(g25,g30)
    c: PointOnObject(g26,g30)
    c: PointOnObject(g27,g30)
    c: PointOnObject(g28,g30)
    c: PointOnObject(g29,g30)
    c: Coincident(g30,g1)
    c: PointOnObject(g31,g0)
    c: DistanceY(g-1,g31) = 5
    c: Equal(g16,g9)
    c: Equal(g9,g30)
    c: Equal(g30,g23)
    c: DistanceX(g11,g13) = 4.2
    c: DistanceX(g2,g2) = 80
    c: DistanceX(g1,g1) = 5.4
    c: Horizontal(g2)
    c: Symmetric(g2,g2,g31)
    c: Coincident(g2,g16)
    c: Vertical(g11)
    c: Vertical(g19)
    c: Coincident(g23,g2)
    c: Vertical(g8)
    c: Vertical(g29)
    c: DistanceY(g-1,g1) = 68.5
FEATURE [PartDesign::Pocket] Pocket014  label="BBToMCP_HexSunk"
  BaseFeature = -> Pocket012
  Length = 1.8
  Length2 = 100
  Placement = pos=(0,0,0) rot=(1,0,0;1.5708rad)
  Profile = -> Sketch024
  Type = 0
  expr: Length = <<params>>.bbtomcp_hex_sunk_height
FEATURE [Sketcher::SketchObject] Sketch025  label="Sketch_BattBToMCP_HexSlot"
  FullyConstrained = true
  MapMode = 5
  Placement = pos=(0,0,13.1) rot=(0,0,1;0rad)
  Support = -> [DatumPlane005]
  expr: Constraints[52] = <<params>>.bbtomcp_hole_loc_leng
  expr: Constraints[56] = <<params>>.m2_nut_clear_flat
  expr: Constraints[97] = <<params>>.bbtomcp_hole_space_width
  expr: Constraints[105] = <<params>>.bbtomcp_rear_hole_spacing_width
  expr: Constraints[106] = <<params>>.bbtomcp_hole_space_leng - <<params>>.bbtomcp_rear_hole_offset_leng
  sketch-geometry (38):
    g0: LineSegment StartX=0 StartY=0 StartZ=0 EndX=0 EndY=68.5 EndZ=0
    g1: LineSegment StartX=-2.7 StartY=68.5 StartZ=0 EndX=2.7 EndY=68.5 EndZ=0
    g2: LineSegment StartX=-40 StartY=5 StartZ=0 EndX=40 EndY=5 EndZ=0
    g3: LineSegment StartX=2.7 StartY=66.0751 StartZ=0 EndX=4.8 EndY=67.2876 EndZ=0
    g4: LineSegment StartX=4.8 StartY=67.2876 StartZ=0 EndX=4.8 EndY=69.7124 EndZ=0
    g5: LineSegment StartX=0.6 StartY=69.7124 StartZ=0 EndX=0.6 EndY=67.2876 EndZ=0
    g6: LineSegment StartX=0.6 StartY=67.2876 StartZ=0 EndX=2.7 EndY=66.0751 EndZ=0
    g7: Circle CenterX=2.7 CenterY=68.5 CenterZ=0 NormalX=0 NormalY=0 NormalZ=1 AngleXU=0 Radius=2.42487
    g8: LineSegment StartX=40 StartY=7.42487 StartZ=0 EndX=37.9 EndY=6.21244 EndZ=0
    g9: LineSegment StartX=37.9 StartY=6.21244 StartZ=0 EndX=37.9 EndY=3.78756 EndZ=0
    g10: LineSegment StartX=42.1 StartY=3.78756 StartZ=0 EndX=42.1 EndY=6.21244 EndZ=0
    g11: LineSegment StartX=42.1 StartY=6.21244 StartZ=0 EndX=40 EndY=7.42487 EndZ=0
    g12: Circle CenterX=40 CenterY=5 CenterZ=0 NormalX=0 NormalY=0 NormalZ=1 AngleXU=0 Radius=2.42487
    g13: LineSegment StartX=-40 StartY=7.42487 StartZ=0 EndX=-42.1 EndY=6.21244 EndZ=0
    g14: LineSegment StartX=-42.1 StartY=6.21244 StartZ=0 EndX=-42.1 EndY=3.78756 EndZ=0
    g15: LineSegment StartX=-37.9 StartY=3.78756 StartZ=0 EndX=-37.9 EndY=6.21244 EndZ=0
    g16: LineSegment StartX=-37.9 StartY=6.21244 StartZ=0 EndX=-40 EndY=7.42487 EndZ=0
    g17: Circle CenterX=-40 CenterY=5 CenterZ=0 NormalX=0 NormalY=0 NormalZ=1 AngleXU=0 Radius=2.42487
    g18: LineSegment StartX=-2.7 StartY=66.0751 StartZ=0 EndX=-0.6 EndY=67.2876 EndZ=0
    g19: LineSegment StartX=-0.6 StartY=67.2876 StartZ=0 EndX=-0.6 EndY=69.7124 EndZ=0
    g20: LineSegment StartX=-4.8 StartY=69.7124 StartZ=0 EndX=-4.8 EndY=67.2876 EndZ=0
    g21: LineSegment StartX=-4.8 StartY=67.2876 StartZ=0 EndX=-2.7 EndY=66.0751 EndZ=0
    g22: Circle CenterX=-2.7 CenterY=68.5 CenterZ=0 NormalX=0 NormalY=0 NormalZ=1 AngleXU=0 Radius=2.42487
    g23: GeomPoint X=0 Y=5 Z=0
    g24: LineSegment StartX=37.9 StartY=3.78756 StartZ=0 EndX=37.9 EndY=-16.2124 EndZ=0
    g25: LineSegment StartX=42.1 StartY=3.78756 StartZ=0 EndX=42.1 EndY=-16.2124 EndZ=0
    g26: LineSegment StartX=37.9 StartY=-16.2124 StartZ=0 EndX=42.1 EndY=-16.2124 EndZ=0
    g27: LineSegment StartX=-42.1 StartY=3.78756 StartZ=0 EndX=-42.1 EndY=-16.2124 EndZ=0
    g28: LineSegment StartX=-37.9 StartY=3.78756 StartZ=0 EndX=-37.9 EndY=-16.2124 EndZ=0
    g29: LineSegment StartX=-42.1 StartY=-16.2124 StartZ=0 EndX=-37.9 EndY=-16.2124 EndZ=0
    g30: LineSegment StartX=-37.9 StartY=-16.2124 StartZ=0 EndX=37.9 EndY=-16.2124 EndZ=0
    g31: LineSegment StartX=0.6 StartY=69.7124 StartZ=0 EndX=0.6 EndY=89.7124 EndZ=0
    g32: LineSegment StartX=4.8 StartY=69.7124 StartZ=0 EndX=4.8 EndY=89.7124 EndZ=0
    g33: LineSegment StartX=0.6 StartY=89.7124 StartZ=0 EndX=4.8 EndY=89.7124 EndZ=0
    g34: LineSegment StartX=-4.8 StartY=69.7124 StartZ=0 EndX=-4.8 EndY=89.7124 EndZ=0
    g35: LineSegment StartX=-0.6 StartY=69.7124 StartZ=0 EndX=-0.6 EndY=89.7124 EndZ=0
    g36: LineSegment StartX=-4.8 StartY=89.7124 StartZ=0 EndX=-0.6 EndY=89.7124 EndZ=0
    g37: LineSegment StartX=-0.6 StartY=89.7124 StartZ=0 EndX=0.6 EndY=89.7124 EndZ=0
  constraints (107):
    c: Coincident(g0,g-1)
    c: PointOnObject(g0,g-2)
    c: Horizontal(g1)
    c: Symmetric(g1,g1,g0)
    c: Horizontal(g2)
    c: Coincident(g3,g4)
    c: Coincident(g5,g6)
    c: Coincident(g6,g3)
    c: Equal(g3,g4)
    c: Equal(g3,g5)
    c: Equal(g3,g6)
    c: PointOnObject(g3,g7)
    c: PointOnObject(g4,g7)
    c: PointOnObject(g5,g7)
    c: PointOnObject(g5,g7)
    c: PointOnObject(g6,g7)
    c: Coincident(g7,g1)
    c: Coincident(g8,g9)
    c: Coincident(g10,g11)
    c: Coincident(g11,g8)
    c: Equal(g8,g9)
    c: Equal(g8,g10)
    c: Equal(g8,g11)
    c: PointOnObject(g8,g12)
    c: PointOnObject(g9,g12)
    c: PointOnObject(g10,g12)
    c: PointOnObject(g10,g12)
    c: PointOnObject(g11,g12)
    c: Coincident(g13,g14)
    c: Coincident(g15,g16)
    c: Coincident(g16,g13)
    c: Equal(g13,g14)
    c: Equal(g13,g15)
    c: Equal(g13,g16)
    c: PointOnObject(g13,g17)
    c: PointOnObject(g14,g17)
    c: PointOnObject(g15,g17)
    c: PointOnObject(g15,g17)
    c: PointOnObject(g16,g17)
    c: Coincident(g18,g19)
    c: Coincident(g20,g21)
    c: Coincident(g21,g18)
    c: Equal(g18,g19)
    c: Equal(g18,g20)
    c: Equal(g18,g21)
    c: PointOnObject(g18,g22)
    c: PointOnObject(g19,g22)
    c: PointOnObject(g20,g22)
    c: PointOnObject(g20,g22)
    c: PointOnObject(g21,g22)
    c: Coincident(g22,g1)
    c: PointOnObject(g23,g0)
    c: DistanceY(g-1,g23) = 5
    c: Equal(g12,g7)
    c: Equal(g7,g22)
    c: Equal(g22,g17)
    c: DistanceX(g9,g10) = 4.2
    c: Vertical(g9)
    c: Vertical(g14)
    c: Vertical(g19)
    c: Vertical(g4)
    c: Coincident(g24,g9)
    c: Vertical(g24)
    c: Coincident(g25,g10)
    c: Vertical(g25)
    c: Coincident(g26,g24)
    c: Coincident(g26,g25)
    c: Horizontal(g26)
    c: Coincident(g27,g14)
    c: Vertical(g27)
    c: Coincident(g28,g15)
    c: Vertical(g28)
    c: Coincident(g29,g27)
    c: Coincident(g29,g28)
    c: Horizontal(g29)
    c: Coincident(g30,g28)
    c: Coincident(g30,g24)
    c: Horizontal(g30)
    c: Distance(g25) = 20
    c: Coincident(g31,g5)
    c: Vertical(g31)
    c: Coincident(g32,g4)
    c: Vertical(g32)
    c: Coincident(g33,g31)
    c: Coincident(g33,g32)
    c: Horizontal(g33)
    c: Coincident(g34,g20)
    c: Vertical(g34)
    c: Coincident(g35,g19)
    c: Vertical(g35)
    c: Coincident(g36,g34)
    c: Coincident(g36,g35)
    c: Horizontal(g36)
    c: Coincident(g37,g35)
    c: Coincident(g37,g31)
    c: Horizontal(g37)
    c: Equal(g32,g25)
    c: DistanceX(g2,g2) = 80
    c: Vertical(g10)
    c: Coincident(g12,g2)
    c: Coincident(g17,g2)
    c: Vertical(g15)
    c: Symmetric(g2,g2,g23)
    c: Vertical(g5)
    c: Vertical(g20)
    c: DistanceX(g1,g1) = 5.4
    c: DistanceY(g-1,g1) = 68.5
FEATURE [PartDesign::Pocket] Pocket015  label="BBToMCP_HexSlot"
  BaseFeature = -> Pocket014
  Length = 2.3
  Length2 = 100
  Placement = pos=(0,0,0) rot=(1,0,0;1.5708rad)
  Profile = -> Sketch025
  Reversed = true
  Type = 0
  expr: Length = <<params>>.bbtomcp_hex_slot_height
FEATURE [PartDesign::Plane] DatumPlane006  label="Datum_BBToMCP_HeadSunk"
  AttachmentOffset = pos=(0,0,1) rot=(0,0,1;0rad)
  Length = 134.472
  MapMode = 5
  Placement = pos=(0,0,1) rot=(0,0,1;0rad)
  ResizeMode = 0
  Support = -> [XY_Plane003]
  Width = 123.472
  expr: .AttachmentOffset.Base.z = <<params>>.mcp_cent_thick - <<params>>.m2_head_min_depth - 0.2mm
FEATURE [Sketcher::SketchObject] Sketch026  label="Sketch_BattBToMCP_HeadClearHoles"
  FullyConstrained = true
  MapMode = 5
  Placement = pos=(0,0,1) rot=(0,0,1;0rad)
  Support = -> [DatumPlane006]
  expr: Constraints[8] = <<params>>.m2_head_clear_diam
  expr: Constraints[4] = <<params>>.bbtomcp_hole_loc_leng + <<params>>.mcp_cent_overhang
  expr: Constraints[5] = Spreadsheet.bbtomcp_hole_space_width
  expr: Constraints[17] = <<params>>.bbtomcp_hole_space_leng
  sketch-geometry (7):
    g0: LineSegment StartX=0 StartY=0 StartZ=0 EndX=0 EndY=9 EndZ=0
    g1: LineSegment StartX=-40 StartY=9 StartZ=0 EndX=40 EndY=9 EndZ=0
    g2: Circle CenterX=-40 CenterY=9 CenterZ=0 NormalX=0 NormalY=0 NormalZ=1 AngleXU=0 Radius=2.15
    g3: Circle CenterX=40 CenterY=9 CenterZ=0 NormalX=0 NormalY=0 NormalZ=1 AngleXU=0 Radius=2.15
    g4: LineSegment StartX=-40 StartY=9 StartZ=0 EndX=-40 EndY=82 EndZ=0
    g5: LineSegment StartX=40 StartY=9 StartZ=0 EndX=40 EndY=82 EndZ=0
    g6: LineSegment StartX=-40 StartY=82 StartZ=0 EndX=40 EndY=82 EndZ=0
  constraints (18):
    c: Coincident(g0,g-1)
    c: PointOnObject(g0,g-2)
    c: Horizontal(g1)
    c: Symmetric(g1,g1,g0)
    c: DistanceY(g-1,g1) = 9
    c: DistanceX(g1,g1) = 80
    c: Coincident(g2,g1)
    c: Coincident(g3,g1)
    c: Diameter(g3) = 4.3
    c: Equal(g3,g2)
    c: Coincident(g4,g2)
    c: Vertical(g4)
    c: Coincident(g5,g3)
    c: Vertical(g5)
    c: Coincident(g6,g4)
    c: Coincident(g6,g5)
    c: Horizontal(g6)
    c: DistanceY(g3,g5) = 73
FEATURE [PartDesign::Pocket] Pocket016  label="BBToMCP_HeadClearHoles"
  BaseFeature = -> Pocket013
  Length = 5
  Length2 = 100
  Profile = -> Sketch026
  Reversed = true
  Type = 1
FEATURE [PartDesign::Body] Body001  label="PB3D_MuCMtPlate"
  Group = -> [Sketch009,Pad001,Sketch011,Sketch012,Pocket005,Sketch014,Pocket006,Sketch015,Pocket008,Sketch017,Pocket009,Sketch018,Pocket010,Sketch022,Sketch023,Pocket013,DatumPlane006,Sketch026,Pocket016]
  Origin = -> Origin003
  Placement = pos=(0,-4,16) rot=(0,0,1;0rad)
  Tip = -> Pocket016
FEATURE [App::Part] Part001  label="PB3D_MuCMtPart"
  Group = -> [Body001]
  Origin = -> Origin002
  Placement = pos=(0,0,1) rot=(0,0,1;0rad)
FEATURE [Sketcher::SketchObject] Sketch027  label="Sketch_BBToMCP_RearWedcge"
  FullyConstrained = true
  MapMode = 5
  Support = -> [XY_Plane001]
  expr: Constraints[26] = <<params>>.bbtomcp_rear_overhang_leng
  expr: Constraints[29] = <<params>>.bbtomcp_rear_overhang_leng * 4
  expr: Constraints[27] = <<params>>.std_rad
  expr: Constraints[28] = <<params>>.bbtomcp_rear_overhang_width
  expr: Constraints[30] = <<params>>.box_leng_tot * 2
  expr: Constraints[33] = <<params>>.box_leng_tot
  sketch-geometry (15):
    g0: LineSegment StartX=-65 StartY=65 StartZ=0 EndX=-15.6569 EndY=65 EndZ=0
    g1: LineSegment StartX=15.6569 StartY=65 StartZ=0 EndX=65 EndY=65 EndZ=0
    g2: LineSegment StartX=-14.2426 StartY=65.5858 StartZ=0 EndX=-7.41421 EndY=72.4142 EndZ=0
    g3: LineSegment StartX=14.2426 StartY=65.5858 StartZ=0 EndX=7.41421 EndY=72.4142 EndZ=0
    g4: LineSegment StartX=-6 StartY=73 StartZ=0 EndX=6 EndY=73 EndZ=0
    g5: LineSegment StartX=-65 StartY=65 StartZ=0 EndX=-65 EndY=97 EndZ=0
    g6: LineSegment StartX=65 StartY=65 StartZ=0 EndX=65 EndY=97 EndZ=0
    g7: LineSegment StartX=65 StartY=97 StartZ=0 EndX=-65 EndY=97 EndZ=0
    g8: ArcOfCircle CenterX=6 CenterY=71 CenterZ=0 NormalX=0 NormalY=0 NormalZ=1 AngleXU=0 Radius=2 StartAngle=0.785398 EndAngle=1.5708
    g9: ArcOfCircle CenterX=15.6569 CenterY=67 CenterZ=0 NormalX=0 NormalY=0 NormalZ=1 AngleXU=0 Radius=2 StartAngle=3.92699 EndAngle=4.71239
    g10: ArcOfCircle CenterX=-6 CenterY=71 CenterZ=0 NormalX=0 NormalY=0 NormalZ=1 AngleXU=0 Radius=2 StartAngle=1.5708 EndAngle=2.35619
    g11: ArcOfCircle CenterX=-15.6569 CenterY=67 CenterZ=0 NormalX=0 NormalY=0 NormalZ=1 AngleXU=0 Radius=2 StartAngle=4.71239 EndAngle=5.49779
    g12: LineSegment StartX=-14.2426 StartY=65.5858 StartZ=0 EndX=14.2426 EndY=65.5858 EndZ=0
    g13: GeomPoint X=0 Y=97 Z=0
    g14: GeomPoint X=0 Y=73 Z=0
  constraints (36):
    c: Horizontal(g0)
    c: Horizontal(g1)
    c: Horizontal(g4)
    c: Coincident(g5,g0)
    c: Vertical(g5)
    c: Coincident(g6,g1)
    c: Vertical(g6)
    c: Coincident(g7,g6)
    c: Coincident(g7,g5)
    c: Horizontal(g7)
    c: Tangent(g4,g8) = 1.5708
    c: Tangent(g3,g8) = -1.5708
    c: Tangent(g3,g9) = 1.5708
    c: Tangent(g1,g9) = -1.5708
    c: Tangent(g4,g10) = 1.5708
    c: Tangent(g2,g10) = 1.5708
    c: Tangent(g2,g11) = -1.5708
    c: Tangent(g0,g11) = -1.5708
    c: Equal(g9,g8)
    c: Equal(g8,g10)
    c: Equal(g10,g11)
    c: Coincident(g12,g2)
    c: Coincident(g12,g3)
    c: Horizontal(g12)
    c: Angle(g12,g2) = 0.785398
    c: Angle(g3,g12) = 0.785398
    c: DistanceY(g1,g4) = 8
    c: Radius(g9) = 2
    c: DistanceX(g4,g4) = 12
    c: DistanceY(g1,g6) = 32
    c: DistanceX(g5,g6) = 130
    c: PointOnObject(g13,g-2)
    c: Symmetric(g5,g6,g13)
    c: DistanceY(g-1,g1) = 65
    c: PointOnObject(g14,g-2)
    c: Symmetric(g4,g4,g14)
FEATURE [PartDesign::Pocket] Pocket017  label="BBToMCP_RearMtCrop"
  BaseFeature = -> Pocket015
  Length = 7.1
  Length2 = 100
  Placement = pos=(0,0,0) rot=(1,0,0;1.5708rad)
  Profile = -> Sketch027
  Reversed = true
  Type = 1
  expr: Length = <<params>>.box_height_tot - <<params>>.box_foot_height - <<params>>.box_foot_vert_split
FEATURE [Sketcher::SketchObject] Sketch028  label="Sketch_TrimTopMountRear"
  FullyConstrained = true
  MapMode = 5
  Placement = pos=(0,0,17) rot=(0,0,1;0rad)
  Support = -> [DatumPlane002]
  expr: Constraints[26] = <<params>>.box_width + 2 * <<params>>.box_wall_thick + 2 * <<params>>.std_rad
  expr: Constraints[27] = <<params>>.box_leng_tot / 2
  expr: Constraints[25] = <<params>>.box_leng_tot
  expr: Constraints[24] = <<params>>.box_width_tot / 2
  sketch-geometry (11):
    g0: LineSegment StartX=-80 StartY=97.5 StartZ=0 EndX=-36 EndY=97.5 EndZ=0
    g1: LineSegment StartX=-36 StartY=97.5 StartZ=0 EndX=-36 EndY=32.5 EndZ=0
    g2: LineSegment StartX=-36 StartY=32.5 StartZ=0 EndX=-80 EndY=32.5 EndZ=0
    g3: LineSegment StartX=-80 StartY=32.5 StartZ=0 EndX=-80 EndY=97.5 EndZ=0
    g4: LineSegment StartX=36 StartY=97.5 StartZ=0 EndX=80 EndY=97.5 EndZ=0
    g5: LineSegment StartX=80 StartY=97.5 StartZ=0 EndX=80 EndY=32.5 EndZ=0
    g6: LineSegment StartX=80 StartY=32.5 StartZ=0 EndX=36 EndY=32.5 EndZ=0
    g7: LineSegment StartX=36 StartY=32.5 StartZ=0 EndX=36 EndY=97.5 EndZ=0
    g8: LineSegment StartX=-36 StartY=97.5 StartZ=0 EndX=36 EndY=97.5 EndZ=0
    g9: LineSegment StartX=-36 StartY=32.5 StartZ=0 EndX=36 EndY=32.5 EndZ=0
    g10: GeomPoint X=0 Y=32.5 Z=0
  constraints (29):
    c: Coincident(g0,g1)
    c: Coincident(g1,g2)
    c: Coincident(g2,g3)
    c: Coincident(g3,g0)
    c: Horizontal(g0)
    c: Horizontal(g2)
    c: Vertical(g1)
    c: Vertical(g3)
    c: Coincident(g4,g5)
    c: Coincident(g5,g6)
    c: Coincident(g6,g7)
    c: Coincident(g7,g4)
    c: Horizontal(g4)
    c: Horizontal(g6)
    c: Vertical(g5)
    c: Vertical(g7)
    c: Coincident(g8,g0)
    c: Coincident(g8,g4)
    c: Coincident(g9,g1)
    c: Coincident(g9,g6)
    c: Horizontal(g9)
    c: Horizontal(g8)
    c: PointOnObject(g10,g-2)
    c: Symmetric(g1,g6,g10)
    c: Distance(g6) = 44
    c: Distance(g5) = 65
    c: DistanceX(g1,g6) = 72
    c: DistanceY(g-1,g6) = 32.5
    c: Equal(g6,g2)
FEATURE [PartDesign::Pocket] Pocket018  label="TrimRearTopBracket"
  BaseFeature = -> Pocket017
  Length = 8.2
  Length2 = 100
  Placement = pos=(0,0,0) rot=(1,0,0;1.5708rad)
  Profile = -> Sketch028
  Type = 0
  expr: Length = <<params>>.box_height_tot - <<params>>.box_foot_height - <<params>>.box_foot_vert_split / 2
FEATURE [PartDesign::Body] Body  label="PB3D_BatBox"
  Group = -> [Sketch,Pad,Sketch001,Pocket,Sketch002,DatumPlane,DatumPlane001,Sketch004,Sketch005,Sketch006,Pocket001,Pocket002,Pocket003,DatumPlane002,Sketch007,Pocket004,Sketch008,Pocket007,DatumPlane003,Sketch020,Sketch021,Pocket012,DatumPlane004,DatumPlane005,Sketch024,Pocket014,Sketch025,Pocket015,Sketch027,Pocket017,Sketch028,Pocket018]
  Origin = -> Origin001
  Tip = -> Pocket018
FEATURE [App::Part] Part  label="PB3D_BatBoxPart"
  Group = -> [Body]
  Origin = -> Origin
FEATURE [Mesh::Feature] Mesh  label="PB3D_BatBox (Meshed)"
FEATURE [Mesh::Feature] Mesh001  label="PB3D_MuCMtPlate (Meshed)"
